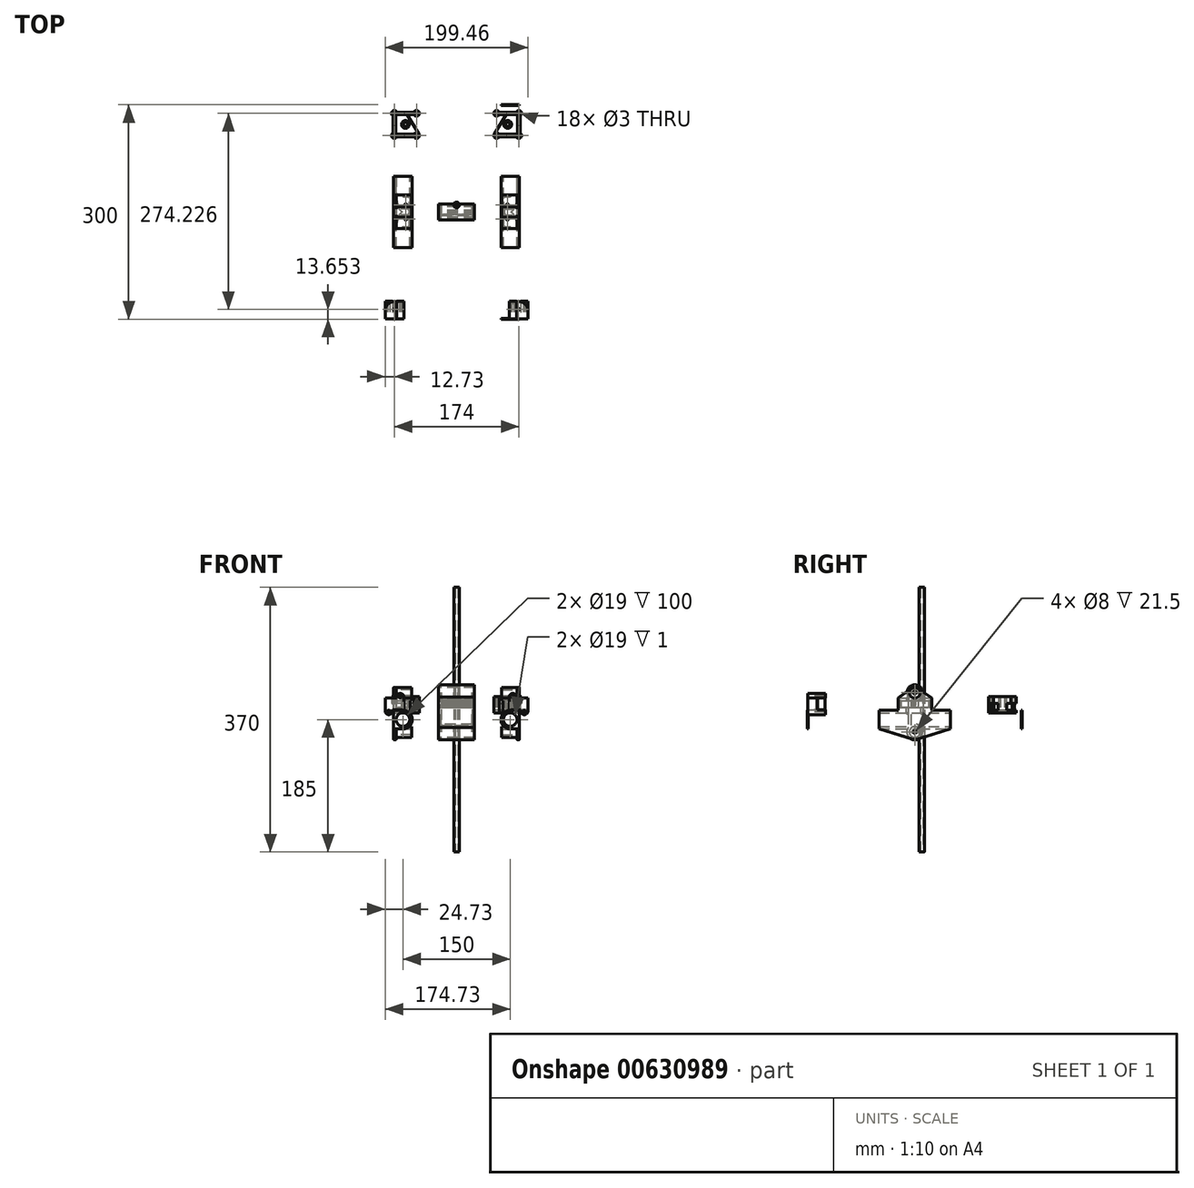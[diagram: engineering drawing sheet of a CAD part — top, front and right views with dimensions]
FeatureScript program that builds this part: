
annotation { "Feature Type Name" : "Feature", "Feature Type Description" : "" }
export const myFeature = defineFeature(function(context is Context, id is Id, definition is map)
    precondition{}
    {
        {
            assignVariable(context, id + "F0", {"variableType" : VariableType.LENGTH, "name" : "Largo", "lengthValue" : 100 * mm});
        }
        {
            assignVariable(context, id + "F1", {"variableType" : VariableType.LENGTH, "name" : "Espesor", "lengthValue" : 3.5 * mm});
        }
        {
            var Q0;
            Q0=qCreatedBy(makeId("Front.planeOp"),FACE);
            var sketch = newSketch(context, id + "F2", { "sketchPlane" : qUnion([Q0])});
            skCircle(sketch, "E0", {"center": v(-75, 0) * mm, "radius": 9.5 * mm});
            skCircle(sketch, "E1", {"center": v(75, 0) * mm, "radius": 9.5 * mm});
            skLineSegment(sketch, "E2", {"start": v(-75, 0) * mm, "end": v(0, 0) * mm, "construction": true});
            skLineSegment(sketch, "E3", {"start": v(0, 0) * mm, "end": v(75, 0) * mm, "construction": true});
            skCircle(sketch, "E4", {"center": v(75, 0) * mm, "radius": 13 * mm, "construction": true});
            skLineSegment(sketch, "E5", {"start": v(88, 0) * mm, "end": v(88, 13) * mm});
            skLineSegment(sketch, "E6", {"start": v(88, 0) * mm, "end": v(88, -13) * mm});
            skLineSegment(sketch, "E7", {"start": v(88, -13) * mm, "end": v(84, -13) * mm});
            skLineSegment(sketch, "E8", {"start": v(84, -13) * mm, "end": v(84, -13) * mm});
            skLineSegment(sketch, "E9", {"start": v(84, -13) * mm, "end": v(75, -13) * mm});
            skLineSegment(sketch, "E10", {"start": v(75, 13) * mm, "end": v(84, 13) * mm});
            skLineSegment(sketch, "E11", {"start": v(84, 13) * mm, "end": v(84, 13) * mm});
            skLineSegment(sketch, "E12", {"start": v(84, 13) * mm, "end": v(88, 13) * mm});
            skArc(sketch, "E13", {"start": v(75, 13) * mm, "mid": v(62, 0) * mm, "end": v(75, -13) * mm});
            skSolve(sketch);
        }
        {
            var Q0;
            Q0=makeQuery(id+"F2.imprint","IMPRINT",FACE,{"disambiguationData":[TD([[makeQuery(id+"F2.imprint","IMPRINT",EDGE,{"derivedFrom":sQuery(id+"F2.wireOp",EDGE,"E1")}),-1.0]])]});
            extrude(context, id + "F3", {"entities" : qUnion([Q0]), "depth" : getVariable(context, 'Largo'), "offsetDistance" : 25 * mm, "symmetric" : true});
        }
        {
            var Q0;
            Q0=makeQuery(id+"F3.opExtrude","SWEPT_FACE",FACE,{"disambiguationData":[OSD([sQuery(id+"F2.wireOp",EDGE,"E5"),sQuery(id+"F2.wireOp",EDGE,"E6")])]});
            var sketch = newSketch(context, id + "F4", { "sketchPlane" : qUnion([Q0])});
            skCircle(sketch, "E14", {"center": v(0, 37.6) * mm, "radius": 2 * mm});
            skCircle(sketch, "E15", {"center": v(0, -17.4) * mm, "radius": 2 * mm});
            skCircle(sketch, "E16", {"center": v(0, -17.4) * mm, "radius": 4 * mm});
            skCircle(sketch, "E17", {"center": v(0, -17.4) * mm, "radius": 7.5 * mm});
            skCircle(sketch, "E18", {"center": v(0, -17.4) * mm, "radius": 10.5 * mm});
            skCircle(sketch, "E19", {"center": v(0, 37.6) * mm, "radius": 4 * mm});
            skCircle(sketch, "E20", {"center": v(0, 37.6) * mm, "radius": 7.5 * mm});
            skCircle(sketch, "E21", {"center": v(0, 37.6) * mm, "radius": 10.5 * mm});
            skLineSegment(sketch, "E22", {"start": v(-50, -13) * mm, "end": v(-3.09, -27.44) * mm});
            skLineSegment(sketch, "E23", {"start": v(50, -13) * mm, "end": v(3.09, -27.44) * mm});
            skLineSegment(sketch, "E24", {"start": v(-50, 13) * mm, "end": v(-6.33, 45.98) * mm});
            skLineSegment(sketch, "E25", {"start": v(50, 13) * mm, "end": v(6.33, 45.98) * mm});
            skLineSegment(sketch, "E26", {"start": v(-7.5, 37.6) * mm, "end": v(-7.5, 28.16) * mm});
            skLineSegment(sketch, "E27", {"start": v(-7.5, 28.16) * mm, "end": v(7.5, 28.16) * mm});
            skLineSegment(sketch, "E28", {"start": v(7.5, 37.6) * mm, "end": v(7.5, 28.16) * mm});
            skSolve(sketch);
        }
        {
            var Q0;
            {var subQ0=sQuery(id+"F4.wireOp",EDGE,"E24");Q0=makeQuery(id+"F4.imprint","IMPRINT",FACE,{"disambiguationData":[TD([[makeQuery(id+"F4.imprint","IMPRINT",EDGE,{"derivedFrom":subQ0}),-1.0]])]});}
            var Q1;
            Q1=makeQuery(id+"F4.imprint","IMPRINT",FACE,{"disambiguationData":[TD([[makeQuery(id+"F4.imprint","IMPRINT",EDGE,{"derivedFrom":sQuery(id+"F4.wireOp",EDGE,"E20")}),-1.0]])]});
            var Q2;
            Q2=makeQuery(id+"F4.imprint","IMPRINT",FACE,{"disambiguationData":[TD([[makeQuery(id+"F4.imprint","IMPRINT",EDGE,{"derivedFrom":sQuery(id+"F4.wireOp",EDGE,"E19")}),-1.0]])]});
            var Q3;
            Q3=makeQuery(id+"F4.imprint","IMPRINT",FACE,{"disambiguationData":[TD([[makeQuery(id+"F4.imprint","IMPRINT",EDGE,{"derivedFrom":sQuery(id+"F4.wireOp",EDGE,"E14")}),-1.0]])]});
            var Q4;
            {var subQ0=sQuery(id+"F4.wireOp",EDGE,"E22");Q4=makeQuery(id+"F4.imprint","IMPRINT",FACE,{"disambiguationData":[TD([[makeQuery(id+"F4.imprint","IMPRINT",EDGE,{"derivedFrom":subQ0}),1.0]])]});}
            var Q5;
            Q5=makeQuery(id+"F4.imprint","IMPRINT",FACE,{"disambiguationData":[TD([[makeQuery(id+"F4.imprint","IMPRINT",EDGE,{"derivedFrom":sQuery(id+"F4.wireOp",EDGE,"E16")}),-1.0]])]});
            var Q6;
            Q6=makeQuery(id+"F4.imprint","IMPRINT",FACE,{"disambiguationData":[TD([[makeQuery(id+"F4.imprint","IMPRINT",EDGE,{"derivedFrom":sQuery(id+"F4.wireOp",EDGE,"E15")}),-1.0]])]});
            var Q7;
            {var subQ0=sQuery(id+"F4.wireOp",EDGE,"E23");Q7=makeQuery(id+"F4.imprint","IMPRINT",FACE,{"disambiguationData":[TD([[makeQuery(id+"F4.imprint","IMPRINT",EDGE,{"derivedFrom":subQ0}),-1.0]])]});}
            var Q8;
            {var subQ0=sQuery(id+"F4.wireOp",EDGE,"E18");var subQ4=makeQuery(id+"F4.imprint","INTERSECT",VERTEX,{"derivedFrom":[subQ0,sQuery(id+"F4.wireOp",EDGE,"E22")]});Q8=makeQuery(id+"F4.imprint","IMPRINT",FACE,{"disambiguationData":[TD([[makeQuery(id+"F4.imprint","IMPRINT",EDGE,{"disambiguationData":[TD([[subQ4,-1.0]])],"derivedFrom":subQ0}),1.0]])]});}
            var Q9;
            {var subQ0=sQuery(id+"F4.wireOp",EDGE,"E26");var subQ1=sQuery(id+"F4.wireOp",EDGE,"E21");var subQ2=makeQuery(id+"F4.imprint","INTERSECT",VERTEX,{"derivedFrom":[subQ1,subQ0]});Q9=makeQuery(id+"F4.imprint","IMPRINT",FACE,{"disambiguationData":[TD([[makeQuery(id+"F4.imprint","IMPRINT",EDGE,{"disambiguationData":[TD([[subQ2,-1.0]])],"derivedFrom":subQ1}),-1.0]])]});}
            var Q10;
            {var subQ0=sQuery(id+"F4.wireOp",EDGE,"E27");var subQ1=sQuery(id+"F4.wireOp",EDGE,"E21");var subQ2=makeQuery(id+"F4.imprint","INTERSECT",VERTEX,{"disambiguationData":[OD(0.0)],"derivedFrom":[subQ1,subQ0]});Q10=makeQuery(id+"F4.imprint","IMPRINT",FACE,{"disambiguationData":[TD([[makeQuery(id+"F4.imprint","IMPRINT",EDGE,{"disambiguationData":[TD([[subQ2,-1.0]])],"derivedFrom":subQ1}),1.0]])]});}
            var Q11;
            {var subQ0=sQuery(id+"F4.wireOp",EDGE,"E27");var subQ1=sQuery(id+"F4.wireOp",EDGE,"E21");var subQ2=makeQuery(id+"F4.imprint","INTERSECT",VERTEX,{"disambiguationData":[OD(1.0)],"derivedFrom":[subQ1,subQ0]});Q11=makeQuery(id+"F4.imprint","IMPRINT",FACE,{"disambiguationData":[TD([[makeQuery(id+"F4.imprint","IMPRINT",EDGE,{"disambiguationData":[TD([[subQ2,-1.0]])],"derivedFrom":subQ1}),-1.0]])]});}
            extrude(context, id + "F5", {"entities" : qUnion([Q0, Q1, Q2, Q3, Q4, Q5, Q6, Q7, Q8, Q9, Q10, Q11]), "operationType" : NewBodyOperationType.ADD, "oppositeDirection" : true, "depth" : getVariable(context, 'Espesor'), "offsetDistance" : 25 * mm});
        }
        {
            var Q0;
            Q0=makeQuery(id+"F3.opExtrude","SWEPT_FACE",FACE,{"disambiguationData":[OSD([sQuery(id+"F2.wireOp",EDGE,"E10"),sQuery(id+"F2.wireOp",EDGE,"E12")])]});
            var sketch = newSketch(context, id + "F6", { "sketchPlane" : qUnion([Q0])});
            skLineSegment(sketch, "E29", {"start": v(84.5, 23.5) * mm, "end": v(63, 23.5) * mm});
            skLineSegment(sketch, "E30", {"start": v(84.5, -23.5) * mm, "end": v(63, -23.5) * mm});
            skLineSegment(sketch, "E31", {"start": v(63, -23.5) * mm, "end": v(63, 23.5) * mm});
            skLineSegment(sketch, "E32", {"start": v(84.5, 23.5) * mm, "end": v(84.5, 0) * mm});
            skLineSegment(sketch, "E33", {"start": v(84.5, 0) * mm, "end": v(84.5, -23.5) * mm});
            skLineSegment(sketch, "E34.bottom", {"start": v(84.5, 10) * mm, "end": v(71, 10) * mm, "construction": true});
            skLineSegment(sketch, "E34.top", {"start": v(84.5, -10) * mm, "end": v(71, -10) * mm, "construction": true});
            skLineSegment(sketch, "E34.left", {"start": v(84.5, 10) * mm, "end": v(84.5, -10) * mm});
            skLineSegment(sketch, "E34.right", {"start": v(71, 10) * mm, "end": v(71, -10) * mm, "construction": true});
            skPoint(sketch, "E34.middle", {"position": v(77.75, 0) * mm});
            skCircle(sketch, "E35", {"center": v(71, 10) * mm, "radius": 9 * mm, "construction": true});
            skCircle(sketch, "E36", {"center": v(71, -10) * mm, "radius": 9 * mm, "construction": true});
            skCircle(sketch, "E37", {"center": v(71, 10) * mm, "radius": 6 * mm, "construction": true});
            skCircle(sketch, "E38", {"center": v(71, -10) * mm, "radius": 6 * mm, "construction": true});
            skCircle(sketch, "E39", {"center": v(71, -10) * mm, "radius": 1.5 * mm});
            skCircle(sketch, "E40", {"center": v(71, 10) * mm, "radius": 1.5 * mm});
            skLineSegment(sketch, "E41", {"start": v(65, -23.5) * mm, "end": v(65, 23.5) * mm});
            skSolve(sketch);
        }
        {
            var Q0;
            {var subQ4=sQuery(id+"F6.wireOp",EDGE,"E41");Q0=makeQuery(id+"F6.imprint","IMPRINT",FACE,{"disambiguationData":[TD([[makeQuery(id+"F6.imprint","IMPRINT",EDGE,{"derivedFrom":subQ4}),-1.0]])]});}
            var Q1;
            {var subQ0=sQuery(id+"F6.wireOp",EDGE,"E32");Q1=makeQuery(id+"F6.imprint","IMPRINT",FACE,{"disambiguationData":[TD([[makeQuery(id+"F6.imprint","IMPRINT",EDGE,{"derivedFrom":subQ0}),1.0]])]});}
            extrude(context, id + "F7", {"entities" : qUnion([Q0, Q1]), "operationType" : NewBodyOperationType.ADD, "oppositeDirection" : true, "depth" : getVariable(context, 'Espesor'), "offsetDistance" : 25 * mm, "hasSecondDirection" : true, "secondDirectionOppositeDirection" : false, "secondDirectionDepth" : 4 * mm});
        }
        {
            var Q0;
            {var subQ0=sQuery(id+"F6.wireOp",EDGE,"E39");var subQ1=makeQuery(id+"F3.opExtrude","SWEPT_EDGE",EDGE,{"disambiguationData":[OSD([sQuery(id+"F2.wireOp",EDGE,"E10"),sQuery(id+"F2.wireOp",EDGE,"E13")])]});var subQ2=makeQuery(id+"F6.imprint","INTERSECT",VERTEX,{"disambiguationData":[OD(0.0)],"derivedFrom":[subQ1,subQ0]});Q0=makeQuery(id+"F6.imprint","IMPRINT",FACE,{"disambiguationData":[TD([[makeQuery(id+"F6.imprint","IMPRINT",EDGE,{"disambiguationData":[TD([[subQ2,-1.0]])],"derivedFrom":subQ0}),1.0]])]});}
            var Q1;
            {var subQ0=sQuery(id+"F6.wireOp",EDGE,"E39");var subQ1=makeQuery(id+"F3.opExtrude","SWEPT_EDGE",EDGE,{"disambiguationData":[OSD([sQuery(id+"F2.wireOp",EDGE,"E10"),sQuery(id+"F2.wireOp",EDGE,"E13")])]});var subQ2=makeQuery(id+"F6.imprint","INTERSECT",VERTEX,{"disambiguationData":[OD(0.0)],"derivedFrom":[subQ1,subQ0]});Q1=makeQuery(id+"F6.imprint","IMPRINT",FACE,{"disambiguationData":[TD([[makeQuery(id+"F6.imprint","IMPRINT",EDGE,{"disambiguationData":[TD([[subQ2,1.0]])],"derivedFrom":subQ0}),1.0]])]});}
            var Q2;
            {var subQ0=sQuery(id+"F6.wireOp",EDGE,"E40");var subQ1=makeQuery(id+"F3.opExtrude","SWEPT_EDGE",EDGE,{"disambiguationData":[OSD([sQuery(id+"F2.wireOp",EDGE,"E10"),sQuery(id+"F2.wireOp",EDGE,"E13")])]});var subQ2=makeQuery(id+"F6.imprint","INTERSECT",VERTEX,{"disambiguationData":[OD(0.0)],"derivedFrom":[subQ1,subQ0]});Q2=makeQuery(id+"F6.imprint","IMPRINT",FACE,{"disambiguationData":[TD([[makeQuery(id+"F6.imprint","IMPRINT",EDGE,{"disambiguationData":[TD([[subQ2,-1.0]])],"derivedFrom":subQ0}),1.0]])]});}
            var Q3;
            {var subQ0=sQuery(id+"F6.wireOp",EDGE,"E40");var subQ1=makeQuery(id+"F3.opExtrude","SWEPT_EDGE",EDGE,{"disambiguationData":[OSD([sQuery(id+"F2.wireOp",EDGE,"E10"),sQuery(id+"F2.wireOp",EDGE,"E13")])]});var subQ2=makeQuery(id+"F6.imprint","INTERSECT",VERTEX,{"disambiguationData":[OD(0.0)],"derivedFrom":[subQ1,subQ0]});Q3=makeQuery(id+"F6.imprint","IMPRINT",FACE,{"disambiguationData":[TD([[makeQuery(id+"F6.imprint","IMPRINT",EDGE,{"disambiguationData":[TD([[subQ2,1.0]])],"derivedFrom":subQ0}),1.0]])]});}
            extrude(context, id + "F8", {"entities" : qUnion([Q0, Q1, Q2, Q3]), "operationType" : NewBodyOperationType.REMOVE, "oppositeDirection" : true, "depth" : 5 * mm, "offsetDistance" : 25 * mm});
        }
        {
            var Q0;
            {var subQ0=sQuery(id+"F6.wireOp",EDGE,"E31");Q0=makeQuery(id+"F6.imprint","IMPRINT",FACE,{"disambiguationData":[TD([[makeQuery(id+"F6.imprint","IMPRINT",EDGE,{"derivedFrom":subQ0}),-1.0]])]});}
            var Q1;
            {var subQ0=sQuery(id+"F6.wireOp",EDGE,"E32");Q1=makeQuery(id+"F6.imprint","IMPRINT",FACE,{"disambiguationData":[TD([[makeQuery(id+"F6.imprint","IMPRINT",EDGE,{"derivedFrom":subQ0}),1.0]])]});}
            var Q2;
            Q2=makeQuery(id+"F6.imprint","IMPRINT",FACE,{"disambiguationData":[TD([[makeQuery(id+"F6.imprint","IMPRINT",EDGE,{"derivedFrom":sQuery(id+"F6.wireOp",EDGE,"E39")}),-1.0]])]});
            extrude(context, id + "F9", {"entities" : qUnion([Q0, Q1, Q2]), "operationType" : NewBodyOperationType.ADD, "depth" : 17 * mm, "offsetDistance" : 25 * mm, "hasSecondDirection" : true, "secondDirectionOppositeDirection" : false, "secondDirectionDepth" : 13.5 * mm});
        }
        {
            var Q0;
            Q0=makeQuery(id+"F2.imprint","IMPRINT",FACE,{"disambiguationData":[TD([[makeQuery(id+"F2.imprint","IMPRINT",EDGE,{"derivedFrom":sQuery(id+"F2.wireOp",EDGE,"E1")}),-1.0]])]});
            extrude(context, id + "F10", {"entities" : qUnion([Q0]), "depth" : 150 * mm, "offsetDistance" : 25 * mm, "hasSecondDirection" : true, "secondDirectionOppositeDirection" : false, "secondDirectionDepth" : 149 * mm});
        }
        {
            var Q0;
            Q0=makeQuery(id+"F2.imprint","IMPRINT",FACE,{"disambiguationData":[TD([[makeQuery(id+"F2.imprint","IMPRINT",EDGE,{"derivedFrom":sQuery(id+"F2.wireOp",EDGE,"E1")}),-1.0]])]});
            extrude(context, id + "F11", {"entities" : qUnion([Q0]), "oppositeDirection" : true, "depth" : 150 * mm, "offsetDistance" : 25 * mm, "hasSecondDirection" : true, "secondDirectionOppositeDirection" : true, "secondDirectionDepth" : 149 * mm});
        }
        {
            var Q0;
            Q0=makeQuery(id+"F10.opExtrude","SWEPT_FACE",FACE,{"disambiguationData":[OSD([sQuery(id+"F2.wireOp",EDGE,"E10"),sQuery(id+"F2.wireOp",EDGE,"E12")])]});
            var sketch = newSketch(context, id + "F12", { "sketchPlane" : qUnion([Q0])});
            skPoint(sketch, "E42", {"position": v(86.73, -136.35) * mm});
            skPoint(sketch, "E43", {"position": v(86.73, -7.67) * mm});
            skLineSegment(sketch, "E44", {"start": v(99.73, -149.85) * mm, "end": v(73.73, -149.85) * mm});
            skLineSegment(sketch, "E45", {"start": v(73.73, -149.85) * mm, "end": v(73.73, -136.35) * mm});
            skLineSegment(sketch, "E46", {"start": v(99.73, -149.85) * mm, "end": v(99.73, -136.35) * mm});
            skCircle(sketch, "E47", {"center": v(86.73, -136.35) * mm, "radius": 9 * mm, "construction": true});
            skArc(sketch, "E48", {"start": v(96.73, -136.35) * mm, "mid": v(86.73, -146.35) * mm, "end": v(76.73, -136.35) * mm});
            skCircle(sketch, "E49", {"center": v(86.73, -136.35) * mm, "radius": 1.5 * mm});
            skArc(sketch, "E50", {"start": v(75.73, -136.35) * mm, "mid": v(86.73, -125.35) * mm, "end": v(97.73, -136.35) * mm, "construction": true});
            skLineSegment(sketch, "E51", {"start": v(76.73, -136.35) * mm, "end": v(76.73, -129.94) * mm});
            skPoint(sketch, "E52", {"position": v(77, -10) * mm});
            skLineSegment(sketch, "E53", {"start": v(76.73, -136.35) * mm, "end": v(76.73, -149.85) * mm, "construction": true});
            skLineSegment(sketch, "E54", {"start": v(96.73, -136.35) * mm, "end": v(96.73, -149.85) * mm, "construction": true});
            skArc(sketch, "E55", {"start": v(99.73, -136.35) * mm, "mid": v(86.73, -125.35) * mm, "end": v(73.73, -136.35) * mm});
            skLineSegment(sketch, "E56", {"start": v(96.73, -136.35) * mm, "end": v(96.73, -129.94) * mm});
            skSolve(sketch);
        }
        {
            var Q0;
            {var subQ5=sQuery(id+"F12.wireOp",EDGE,"E45");Q0=makeQuery(id+"F12.imprint","IMPRINT",FACE,{"disambiguationData":[TD([[makeQuery(id+"F12.imprint","IMPRINT",EDGE,{"derivedFrom":subQ5}),-1.0]])]});}
            var Q1;
            Q1=makeQuery(id+"F12.imprint","IMPRINT",FACE,{"disambiguationData":[TD([[makeQuery(id+"F12.imprint","IMPRINT",EDGE,{"derivedFrom":sQuery(id+"F12.wireOp",EDGE,"E48")}),-1.0]])]});
            var Q2;
            {var subQ0=sQuery(id+"F12.wireOp",EDGE,"E46");Q2=makeQuery(id+"F12.imprint","IMPRINT",FACE,{"disambiguationData":[TD([[makeQuery(id+"F12.imprint","IMPRINT",EDGE,{"derivedFrom":subQ0}),1.0]])]});}
            var Q3;
            {var subQ2=sQuery(id+"F12.wireOp",EDGE,"E48");Q3=makeQuery(id+"F12.imprint","IMPRINT",FACE,{"disambiguationData":[TD([[makeQuery(id+"F12.imprint","IMPRINT",EDGE,{"derivedFrom":subQ2}),1.0]])]});}
            var Q4;
            {var subQ0=sQuery(id+"F12.wireOp",EDGE,"E53");var subQ1=sQuery(id+"F12.wireOp",EDGE,"E44");var subQ2=makeQuery(id+"F12.imprint","INTERSECT",VERTEX,{"derivedFrom":[subQ1,subQ0]});Q4=makeQuery(id+"F12.imprint","IMPRINT",FACE,{"disambiguationData":[TD([[makeQuery(id+"F12.imprint","IMPRINT",EDGE,{"disambiguationData":[TD([[subQ2,1.0]])],"derivedFrom":subQ1}),-1.0]])]});}
            var Q5;
            {var subQ0=sQuery(id+"F12.wireOp",EDGE,"E53");var subQ1=sQuery(id+"F12.wireOp",EDGE,"E44");var subQ2=makeQuery(id+"F12.imprint","INTERSECT",VERTEX,{"derivedFrom":[subQ1,subQ0]});Q5=makeQuery(id+"F12.imprint","IMPRINT",FACE,{"disambiguationData":[TD([[makeQuery(id+"F12.imprint","IMPRINT",EDGE,{"disambiguationData":[TD([[subQ2,-1.0]])],"derivedFrom":subQ1}),-1.0]])]});}
            var Q6;
            {var subQ1=sQuery(id+"F2.wireOp",EDGE,"E12");var subQ4=sQuery(id+"F2.wireOp",EDGE,"E10");var subQ7=makeQuery(id+"F10.opExtrude","CAP_EDGE",EDGE,{"disambiguationData":[OSD([subQ4,subQ1])],"isStart":true});Q6=makeQuery(id+"F12.imprint","IMPRINT",FACE,{"disambiguationData":[TD([[makeQuery(id+"F12.imprint","IMPRINT",EDGE,{"derivedFrom":subQ7}),-1.0]])]});}
            extrude(context, id + "F13", {"entities" : qUnion([Q0, Q1, Q2, Q3, Q4, Q5, Q6]), "operationType" : NewBodyOperationType.ADD, "depth" : 4 * mm, "offsetDistance" : 25 * mm, "hasSecondDirection" : true, "secondDirectionOppositeDirection" : false, "secondDirectionDepth" : 0.5 * mm});
        }
        {
            var Q0;
            {var subQ5=sQuery(id+"F12.wireOp",EDGE,"E45");Q0=makeQuery(id+"F12.imprint","IMPRINT",FACE,{"disambiguationData":[TD([[makeQuery(id+"F12.imprint","IMPRINT",EDGE,{"derivedFrom":subQ5}),-1.0]])]});}
            var Q1;
            {var subQ0=sQuery(id+"F12.wireOp",EDGE,"E46");Q1=makeQuery(id+"F12.imprint","IMPRINT",FACE,{"disambiguationData":[TD([[makeQuery(id+"F12.imprint","IMPRINT",EDGE,{"derivedFrom":subQ0}),1.0]])]});}
            var Q2;
            {var subQ2=sQuery(id+"F12.wireOp",EDGE,"E48");Q2=makeQuery(id+"F12.imprint","IMPRINT",FACE,{"disambiguationData":[TD([[makeQuery(id+"F12.imprint","IMPRINT",EDGE,{"derivedFrom":subQ2}),1.0]])]});}
            var Q3;
            {var subQ0=sQuery(id+"F12.wireOp",EDGE,"E53");var subQ1=sQuery(id+"F12.wireOp",EDGE,"E44");var subQ2=makeQuery(id+"F12.imprint","INTERSECT",VERTEX,{"derivedFrom":[subQ1,subQ0]});Q3=makeQuery(id+"F12.imprint","IMPRINT",FACE,{"disambiguationData":[TD([[makeQuery(id+"F12.imprint","IMPRINT",EDGE,{"disambiguationData":[TD([[subQ2,1.0]])],"derivedFrom":subQ1}),-1.0]])]});}
            var Q4;
            {var subQ1=sQuery(id+"F2.wireOp",EDGE,"E12");var subQ4=sQuery(id+"F2.wireOp",EDGE,"E10");var subQ7=makeQuery(id+"F10.opExtrude","CAP_EDGE",EDGE,{"disambiguationData":[OSD([subQ4,subQ1])],"isStart":true});Q4=makeQuery(id+"F12.imprint","IMPRINT",FACE,{"disambiguationData":[TD([[makeQuery(id+"F12.imprint","IMPRINT",EDGE,{"derivedFrom":subQ7}),-1.0]])]});}
            extrude(context, id + "F14", {"entities" : qUnion([Q0, Q1, Q2, Q3, Q4]), "operationType" : NewBodyOperationType.ADD, "depth" : 13.5 * mm, "offsetDistance" : 25 * mm, "hasSecondDirection" : true, "secondDirectionOppositeDirection" : false, "secondDirectionDepth" : 0.5 * mm});
        }
        {
            var Q0;
            {var subQ5=sQuery(id+"F12.wireOp",EDGE,"E45");Q0=makeQuery(id+"F12.imprint","IMPRINT",FACE,{"disambiguationData":[TD([[makeQuery(id+"F12.imprint","IMPRINT",EDGE,{"derivedFrom":subQ5}),-1.0]])]});}
            var Q1;
            Q1=makeQuery(id+"F12.imprint","IMPRINT",FACE,{"disambiguationData":[TD([[makeQuery(id+"F12.imprint","IMPRINT",EDGE,{"derivedFrom":sQuery(id+"F12.wireOp",EDGE,"E48")}),-1.0]])]});
            var Q2;
            {var subQ0=sQuery(id+"F12.wireOp",EDGE,"E46");Q2=makeQuery(id+"F12.imprint","IMPRINT",FACE,{"disambiguationData":[TD([[makeQuery(id+"F12.imprint","IMPRINT",EDGE,{"derivedFrom":subQ0}),1.0]])]});}
            var Q3;
            {var subQ2=sQuery(id+"F12.wireOp",EDGE,"E48");Q3=makeQuery(id+"F12.imprint","IMPRINT",FACE,{"disambiguationData":[TD([[makeQuery(id+"F12.imprint","IMPRINT",EDGE,{"derivedFrom":subQ2}),1.0]])]});}
            var Q4;
            {var subQ0=sQuery(id+"F12.wireOp",EDGE,"E53");var subQ1=sQuery(id+"F12.wireOp",EDGE,"E44");var subQ2=makeQuery(id+"F12.imprint","INTERSECT",VERTEX,{"derivedFrom":[subQ1,subQ0]});Q4=makeQuery(id+"F12.imprint","IMPRINT",FACE,{"disambiguationData":[TD([[makeQuery(id+"F12.imprint","IMPRINT",EDGE,{"disambiguationData":[TD([[subQ2,1.0]])],"derivedFrom":subQ1}),-1.0]])]});}
            var Q5;
            {var subQ1=sQuery(id+"F2.wireOp",EDGE,"E12");var subQ4=sQuery(id+"F2.wireOp",EDGE,"E10");var subQ7=makeQuery(id+"F10.opExtrude","CAP_EDGE",EDGE,{"disambiguationData":[OSD([subQ4,subQ1])],"isStart":true});Q5=makeQuery(id+"F12.imprint","IMPRINT",FACE,{"disambiguationData":[TD([[makeQuery(id+"F12.imprint","IMPRINT",EDGE,{"derivedFrom":subQ7}),-1.0]])]});}
            extrude(context, id + "F15", {"entities" : qUnion([Q0, Q1, Q2, Q3, Q4, Q5]), "operationType" : NewBodyOperationType.ADD, "depth" : (4 + 9.5 + 3.5) * mm, "offsetDistance" : 25 * mm, "hasSecondDirection" : true, "secondDirectionOppositeDirection" : false, "secondDirectionDepth" : (4 + 9.5) * mm});
        }
        {
            var Q0;
            {var subQ0=sQuery(id+"F12.wireOp",EDGE,"E44");Q0=makeQuery(id+"F15.boolean.opBoolean","MERGE",FACE,{"derivedFrom":[makeQuery(id+"F14.boolean.opBoolean","MERGE",FACE,{"derivedFrom":[makeQuery(id+"F13.opExtrude","SWEPT_FACE",FACE,{"disambiguationData":[OSD([subQ0])]}),makeQuery(id+"F14.opExtrude","SWEPT_FACE",FACE,{"disambiguationData":[OSD([subQ0])]})]}),makeQuery(id+"F15.opExtrude","SWEPT_FACE",FACE,{"disambiguationData":[OSD([subQ0])]})]});}
            var sketch = newSketch(context, id + "F16", { "sketchPlane" : qUnion([Q0])});
            skLineSegment(sketch, "E57", {"start": v(73.73, 31.63) * mm, "end": v(73.73, 30) * mm});
            skLineSegment(sketch, "E58", {"start": v(73.73, 30) * mm, "end": v(83.73, 30) * mm});
            skLineSegment(sketch, "E59", {"start": v(83.73, 30) * mm, "end": v(83.73, 31.63) * mm});
            skCircle(sketch, "E60", {"center": v(78.73, 31.63) * mm, "radius": 1.5 * mm});
            skArc(sketch, "E61", {"start": v(73.73, 31.63) * mm, "mid": v(78.73, 36.63) * mm, "end": v(83.73, 31.63) * mm});
            skPoint(sketch, "E62", {"position": v(75, 0) * mm});
            skLineSegment(sketch, "E63.top", {"start": v(78.73, 11.87) * mm, "end": v(78.95, 11.87) * mm, "construction": true});
            skLineSegment(sketch, "E63.left", {"start": v(78.73, 31.63) * mm, "end": v(78.73, 11.87) * mm, "construction": true});
            skLineSegment(sketch, "E64.bottom", {"start": v(78.73, 11.87) * mm, "end": v(75, 11.87) * mm, "construction": true});
            skLineSegment(sketch, "E64.top", {"start": v(78.73, 0) * mm, "end": v(75, 0) * mm, "construction": true});
            skLineSegment(sketch, "E64.left", {"start": v(78.73, 11.87) * mm, "end": v(78.73, 0) * mm, "construction": true});
            skLineSegment(sketch, "E64.right", {"start": v(75, 11.87) * mm, "end": v(75, 0) * mm, "construction": true});
            skLineSegment(sketch, "E65", {"start": v(89.73, 11.87) * mm, "end": v(89.73, 13.5) * mm});
            skLineSegment(sketch, "E66", {"start": v(89.73, 13.5) * mm, "end": v(99.73, 13.5) * mm});
            skLineSegment(sketch, "E67", {"start": v(99.73, 13.5) * mm, "end": v(99.73, 11.87) * mm});
            skArc(sketch, "E68", {"start": v(99.73, 11.87) * mm, "mid": v(94.73, 6.87) * mm, "end": v(89.73, 11.87) * mm});
            skCircle(sketch, "E69", {"center": v(94.73, 11.87) * mm, "radius": 1.5 * mm});
            skLineSegment(sketch, "E70.bottom", {"start": v(78.73, 11.87) * mm, "end": v(94.73, 11.87) * mm, "construction": true});
            skLineSegment(sketch, "E70.top", {"start": v(78.73, 31.63) * mm, "end": v(94.73, 31.63) * mm, "construction": true});
            skLineSegment(sketch, "E70.left", {"start": v(78.73, 11.87) * mm, "end": v(78.73, 31.63) * mm, "construction": true});
            skLineSegment(sketch, "E70.right", {"start": v(94.73, 11.87) * mm, "end": v(94.73, 31.63) * mm, "construction": true});
            skSolve(sketch);
        }
        {
            var Q0;
            {var subQ2=sQuery(id+"F16.wireOp",EDGE,"E57");Q0=makeQuery(id+"F16.imprint","IMPRINT",FACE,{"disambiguationData":[TD([[makeQuery(id+"F16.imprint","IMPRINT",EDGE,{"derivedFrom":subQ2}),1.0]])]});}
            var Q1;
            {var subQ5=sQuery(id+"F16.wireOp",EDGE,"lFzHnj4Q-87Bt-HTbF-StXR-67TSzxUFeQIK");Q1=makeQuery(id+"F16.imprint","IMPRINT",FACE,{"disambiguationData":[TD([[makeQuery(id+"F16.imprint","IMPRINT",EDGE,{"derivedFrom":subQ5}),1.0]])]});}
            var Q2;
            Q2=makeQuery(id+"F16.imprint","IMPRINT",FACE,{"disambiguationData":[TD([[makeQuery(id+"F16.imprint","IMPRINT",EDGE,{"derivedFrom":sQuery(id+"F16.wireOp",EDGE,"E65")}),-1.0]])]});
            var Q3;
            {var subQ0=sQuery(id+"F16.wireOp",EDGE,"E61");Q3=makeQuery(id+"F16.imprint","IMPRINT",FACE,{"disambiguationData":[TD([[makeQuery(id+"F16.imprint","IMPRINT",EDGE,{"derivedFrom":subQ0}),-1.0]])]});}
            var Q4;
            {var subQ0=sQuery(id+"F16.wireOp",EDGE,"E68");Q4=makeQuery(id+"F16.imprint","IMPRINT",FACE,{"disambiguationData":[TD([[makeQuery(id+"F16.imprint","IMPRINT",EDGE,{"derivedFrom":subQ0}),-1.0]])]});}
            extrude(context, id + "F17", {"entities" : qUnion([Q0, Q1, Q2, Q3, Q4]), "operationType" : NewBodyOperationType.ADD, "oppositeDirection" : true, "depth" : 25 * mm, "offsetDistance" : 25 * mm});
        }
        {
            var Q0;
            {var subQ0=sQuery(id+"F4.wireOp",EDGE,"E16");Q0=makeQuery(id+"F4.imprint","IMPRINT",FACE,{"disambiguationData":[TD([[makeQuery(id+"F4.imprint","IMPRINT",EDGE,{"derivedFrom":subQ0}),-1.0]])]});}
            var Q1;
            {var subQ0=sQuery(id+"F4.wireOp",EDGE,"E17");var subQ1=makeQuery(id+"F3.opExtrude","SWEPT_EDGE",EDGE,{"disambiguationData":[OSD([sQuery(id+"F2.wireOp",EDGE,"E6"),sQuery(id+"F2.wireOp",EDGE,"E7")])]});var subQ2=makeQuery(id+"F4.imprint","INTERSECT",VERTEX,{"disambiguationData":[OD(0.0)],"derivedFrom":[subQ1,subQ0]});Q1=makeQuery(id+"F4.imprint","IMPRINT",FACE,{"disambiguationData":[TD([[makeQuery(id+"F4.imprint","IMPRINT",EDGE,{"disambiguationData":[TD([[subQ2,1.0]])],"derivedFrom":subQ0}),1.0]])]});}
            var Q2;
            Q2=makeQuery(id+"F4.imprint","IMPRINT",FACE,{"disambiguationData":[TD([[makeQuery(id+"F4.imprint","IMPRINT",EDGE,{"derivedFrom":sQuery(id+"F4.wireOp",EDGE,"E19")}),-1.0]])]});
            var Q3;
            {var subQ0=sQuery(id+"F4.wireOp",EDGE,"E26");var subQ1=sQuery(id+"F4.wireOp",EDGE,"E20");var subQ2=makeQuery(id+"F4.imprint","INTERSECT",VERTEX,{"derivedFrom":[subQ1,subQ0]});Q3=makeQuery(id+"F4.imprint","IMPRINT",FACE,{"disambiguationData":[TD([[makeQuery(id+"F4.imprint","IMPRINT",EDGE,{"disambiguationData":[TD([[subQ2,-1.0]])],"derivedFrom":subQ1}),-1.0]])]});}
            var Q4;
            {var subQ0=sQuery(id+"F4.wireOp",EDGE,"E27");var subQ1=sQuery(id+"F4.wireOp",EDGE,"E21");var subQ2=makeQuery(id+"F4.imprint","INTERSECT",VERTEX,{"disambiguationData":[OD(1.0)],"derivedFrom":[subQ1,subQ0]});Q4=makeQuery(id+"F4.imprint","IMPRINT",FACE,{"disambiguationData":[TD([[makeQuery(id+"F4.imprint","IMPRINT",EDGE,{"disambiguationData":[TD([[subQ2,-1.0]])],"derivedFrom":subQ1}),-1.0]])]});}
            var Q5;
            {var subQ0=sQuery(id+"F4.wireOp",EDGE,"E26");var subQ1=sQuery(id+"F4.wireOp",EDGE,"E21");var subQ2=makeQuery(id+"F4.imprint","INTERSECT",VERTEX,{"derivedFrom":[subQ1,subQ0]});Q5=makeQuery(id+"F4.imprint","IMPRINT",FACE,{"disambiguationData":[TD([[makeQuery(id+"F4.imprint","IMPRINT",EDGE,{"disambiguationData":[TD([[subQ2,-1.0]])],"derivedFrom":subQ1}),-1.0]])]});}
            extrude(context, id + "F18", {"entities" : qUnion([Q0, Q1, Q2, Q3, Q4, Q5]), "operationType" : NewBodyOperationType.ADD, "oppositeDirection" : true, "depth" : 25 * mm, "offsetDistance" : 25 * mm});
        }
        {
            var Q0;
            Q0=makeQuery(id+"F11.opExtrude","SWEPT_FACE",FACE,{"disambiguationData":[OSD([sQuery(id+"F2.wireOp",EDGE,"E10"),sQuery(id+"F2.wireOp",EDGE,"E12")])]});
            var sketch = newSketch(context, id + "F19", { "sketchPlane" : qUnion([Q0])});
            skPoint(sketch, "E71", {"position": v(71.5, 10) * mm});
            skPoint(sketch, "E72", {"position": v(77, 10) * mm});
            skPoint(sketch, "E73", {"position": v(71.5, 122.38) * mm});
            skLineSegment(sketch, "E74.bottom", {"start": v(50, 143.88) * mm, "end": v(93, 143.88) * mm});
            skLineSegment(sketch, "E74.top", {"start": v(50, 100.88) * mm, "end": v(93, 100.88) * mm});
            skLineSegment(sketch, "E74.left", {"start": v(50, 143.88) * mm, "end": v(50, 100.88) * mm});
            skLineSegment(sketch, "E74.right", {"start": v(93, 143.88) * mm, "end": v(93, 100.88) * mm});
            skLineSegment(sketch, "E75.bottom", {"start": v(56, 137.88) * mm, "end": v(87, 137.88) * mm, "construction": true});
            skLineSegment(sketch, "E75.top", {"start": v(56, 106.88) * mm, "end": v(87, 106.88) * mm, "construction": true});
            skLineSegment(sketch, "E75.left", {"start": v(56, 137.88) * mm, "end": v(56, 106.88) * mm, "construction": true});
            skLineSegment(sketch, "E75.right", {"start": v(87, 137.88) * mm, "end": v(87, 106.88) * mm, "construction": true});
            skCircle(sketch, "E76", {"center": v(56, 137.88) * mm, "radius": 1.5 * mm});
            skCircle(sketch, "E77", {"center": v(87, 137.88) * mm, "radius": 1.5 * mm});
            skCircle(sketch, "E78", {"center": v(87, 106.88) * mm, "radius": 1.5 * mm});
            skCircle(sketch, "E79", {"center": v(56, 106.88) * mm, "radius": 1.5 * mm});
            skCircle(sketch, "E80", {"center": v(71.5, 122.38) * mm, "radius": 5.5 * mm});
            skCircle(sketch, "E81", {"center": v(71.5, 122.38) * mm, "radius": 7.5 * mm});
            skLineSegment(sketch, "E82", {"start": v(71.5, 122.38) * mm, "end": v(71.5, 10) * mm, "construction": true});
            skCircle(sketch, "E83", {"center": v(87, 137.88) * mm, "radius": 7.5 * mm});
            skCircle(sketch, "E84", {"center": v(87, 137.88) * mm, "radius": 6 * mm});
            skLineSegment(sketch, "E85.bottom", {"start": v(87, 137.88) * mm, "end": v(101, 137.88) * mm, "construction": true});
            skLineSegment(sketch, "E85.top", {"start": v(87, 151.88) * mm, "end": v(101, 151.88) * mm, "construction": true});
            skLineSegment(sketch, "E85.left", {"start": v(87, 137.88) * mm, "end": v(87, 151.88) * mm, "construction": true});
            skLineSegment(sketch, "E85.right", {"start": v(101, 137.88) * mm, "end": v(101, 151.88) * mm, "construction": true});
            skLineSegment(sketch, "E86.bottom", {"start": v(101, 151.88) * mm, "end": v(98.5, 151.88) * mm});
            skLineSegment(sketch, "E86.left", {"start": v(101, 151.88) * mm, "end": v(101, 149.38) * mm});
            skCircle(sketch, "E87", {"center": v(56, 137.88) * mm, "radius": 4 * mm});
            skCircle(sketch, "E88", {"center": v(87, 137.88) * mm, "radius": 4 * mm});
            skCircle(sketch, "E89", {"center": v(87, 106.88) * mm, "radius": 4 * mm});
            skLineSegment(sketch, "E90.bottom", {"start": v(59.6, 136.13) * mm, "end": v(83.4, 136.13) * mm});
            skLineSegment(sketch, "E90.top", {"start": v(59.6, 139.63) * mm, "end": v(83.4, 139.63) * mm});
            skLineSegment(sketch, "E90.left", {"start": v(59.6, 136.13) * mm, "end": v(59.6, 139.63) * mm, "construction": true});
            skLineSegment(sketch, "E90.right", {"start": v(83.4, 136.13) * mm, "end": v(83.4, 139.63) * mm, "construction": true});
            skPoint(sketch, "E90.middle", {"position": v(71.5, 137.88) * mm});
            skLineSegment(sketch, "E91.bottom", {"start": v(85.25, 134.28) * mm, "end": v(88.75, 134.28) * mm, "construction": true});
            skLineSegment(sketch, "E91.top", {"start": v(85.25, 110.48) * mm, "end": v(88.75, 110.48) * mm, "construction": true});
            skLineSegment(sketch, "E91.left", {"start": v(85.25, 134.28) * mm, "end": v(85.25, 110.48) * mm});
            skLineSegment(sketch, "E91.right", {"start": v(88.75, 134.28) * mm, "end": v(88.75, 110.48) * mm});
            skPoint(sketch, "E91.middle", {"position": v(87, 122.38) * mm});
            skCircle(sketch, "E92", {"center": v(87, 137.88) * mm, "radius": 9.5 * mm});
            skCircle(sketch, "E93", {"center": v(87, 106.88) * mm, "radius": 9.5 * mm});
            skCircle(sketch, "E94", {"center": v(56, 106.88) * mm, "radius": 4 * mm});
            skLineSegment(sketch, "E95.bottom", {"start": v(59.6, 105.13) * mm, "end": v(83.4, 105.13) * mm});
            skLineSegment(sketch, "E95.top", {"start": v(59.6, 108.63) * mm, "end": v(83.4, 108.63) * mm});
            skLineSegment(sketch, "E95.left", {"start": v(59.6, 105.13) * mm, "end": v(59.6, 108.63) * mm, "construction": true});
            skLineSegment(sketch, "E95.right", {"start": v(83.4, 105.13) * mm, "end": v(83.4, 108.63) * mm, "construction": true});
            skPoint(sketch, "E95.middle", {"position": v(71.5, 106.88) * mm});
            skCircle(sketch, "E96", {"center": v(71.5, 122.38) * mm, "radius": 3 * mm});
            skLineSegment(sketch, "E97", {"start": v(71.5, 139.63) * mm, "end": v(52.6, 108.98) * mm});
            skSolve(sketch);
        }
        {
            var Q0;
            Q0=makeQuery(id+"F19.imprint","IMPRINT",FACE,{"disambiguationData":[TD([[makeQuery(id+"F19.imprint","IMPRINT",EDGE,{"derivedFrom":sQuery(id+"F19.wireOp",EDGE,"E80")}),1.0]])]});
            var Q1;
            Q1=makeQuery(id+"F19.imprint","IMPRINT",FACE,{"disambiguationData":[TD([[makeQuery(id+"F19.imprint","IMPRINT",EDGE,{"derivedFrom":sQuery(id+"F19.wireOp",EDGE,"E77")}),-1.0]])]});
            var Q2;
            {var subQ0=sQuery(id+"F19.wireOp",EDGE,"E90.top");var subQ1=sQuery(id+"F19.wireOp",EDGE,"E84");var subQ2=makeQuery(id+"F19.imprint","INTERSECT",VERTEX,{"derivedFrom":[subQ1,subQ0]});Q2=makeQuery(id+"F19.imprint","IMPRINT",FACE,{"disambiguationData":[TD([[makeQuery(id+"F19.imprint","IMPRINT",EDGE,{"disambiguationData":[TD([[subQ2,-1.0]])],"derivedFrom":subQ1}),1.0]])]});}
            var Q3;
            {var subQ0=sQuery(id+"F19.wireOp",EDGE,"E91.left");var subQ1=sQuery(id+"F19.wireOp",EDGE,"E84");var subQ2=makeQuery(id+"F19.imprint","INTERSECT",VERTEX,{"derivedFrom":[subQ1,subQ0]});Q3=makeQuery(id+"F19.imprint","IMPRINT",FACE,{"disambiguationData":[TD([[makeQuery(id+"F19.imprint","IMPRINT",EDGE,{"disambiguationData":[TD([[subQ2,-1.0]])],"derivedFrom":subQ1}),1.0]])]});}
            var Q4;
            {var subQ0=sQuery(id+"F19.wireOp",EDGE,"E92");var subQ1=sQuery(id+"F19.wireOp",EDGE,"E91.left");var subQ2=makeQuery(id+"F19.imprint","INTERSECT",VERTEX,{"derivedFrom":[subQ1,subQ0]});Q4=makeQuery(id+"F19.imprint","IMPRINT",FACE,{"disambiguationData":[TD([[makeQuery(id+"F19.imprint","IMPRINT",EDGE,{"disambiguationData":[TD([[subQ2,-1.0]])],"derivedFrom":subQ1}),1.0]])]});}
            var Q5;
            {var subQ0=sQuery(id+"F19.wireOp",EDGE,"E95.bottom");var subQ1=sQuery(id+"F19.wireOp",EDGE,"E89");var subQ2=makeQuery(id+"F19.imprint","INTERSECT",VERTEX,{"derivedFrom":[subQ1,subQ0]});Q5=makeQuery(id+"F19.imprint","IMPRINT",FACE,{"disambiguationData":[TD([[makeQuery(id+"F19.imprint","IMPRINT",EDGE,{"disambiguationData":[TD([[subQ2,1.0]])],"derivedFrom":subQ1}),-1.0]])]});}
            var Q6;
            {var subQ0=sQuery(id+"F19.wireOp",EDGE,"E95.top");var subQ1=sQuery(id+"F19.wireOp",EDGE,"E93");var subQ2=makeQuery(id+"F19.imprint","INTERSECT",VERTEX,{"derivedFrom":[subQ1,subQ0]});Q6=makeQuery(id+"F19.imprint","IMPRINT",FACE,{"disambiguationData":[TD([[makeQuery(id+"F19.imprint","IMPRINT",EDGE,{"disambiguationData":[TD([[subQ2,-1.0]])],"derivedFrom":subQ1}),-1.0]])]});}
            var Q7;
            Q7=makeQuery(id+"F19.imprint","IMPRINT",FACE,{"disambiguationData":[TD([[makeQuery(id+"F19.imprint","IMPRINT",EDGE,{"derivedFrom":sQuery(id+"F19.wireOp",EDGE,"E79")}),-1.0]])]});
            var Q8;
            Q8=makeQuery(id+"F19.imprint","IMPRINT",FACE,{"disambiguationData":[TD([[makeQuery(id+"F19.imprint","IMPRINT",EDGE,{"derivedFrom":sQuery(id+"F19.wireOp",EDGE,"E78")}),-1.0]])]});
            var Q9;
            {var subQ0=sQuery(id+"F19.wireOp",EDGE,"E91.left");var subQ1=sQuery(id+"F19.wireOp",EDGE,"E89");var subQ2=makeQuery(id+"F19.imprint","INTERSECT",VERTEX,{"derivedFrom":[subQ1,subQ0]});Q9=makeQuery(id+"F19.imprint","IMPRINT",FACE,{"disambiguationData":[TD([[makeQuery(id+"F19.imprint","IMPRINT",EDGE,{"disambiguationData":[TD([[subQ2,1.0]])],"derivedFrom":subQ1}),-1.0]])]});}
            var Q10;
            Q10=makeQuery(id+"F19.imprint","IMPRINT",FACE,{"disambiguationData":[TD([[makeQuery(id+"F19.imprint","IMPRINT",EDGE,{"derivedFrom":sQuery(id+"F19.wireOp",EDGE,"E76")}),-1.0]])]});
            var Q11;
            {var subQ0=sQuery(id+"F19.wireOp",EDGE,"E90.bottom");var subQ1=sQuery(id+"F19.wireOp",EDGE,"E87");var subQ2=makeQuery(id+"F19.imprint","INTERSECT",VERTEX,{"derivedFrom":[subQ1,subQ0]});Q11=makeQuery(id+"F19.imprint","IMPRINT",FACE,{"disambiguationData":[TD([[makeQuery(id+"F19.imprint","IMPRINT",EDGE,{"disambiguationData":[TD([[subQ2,-1.0]])],"derivedFrom":subQ1}),-1.0]])]});}
            var Q12;
            {var subQ0=sQuery(id+"F19.wireOp",EDGE,"E90.top");var subQ1=sQuery(id+"F19.wireOp",EDGE,"E83");var subQ2=makeQuery(id+"F19.imprint","INTERSECT",VERTEX,{"derivedFrom":[subQ1,subQ0]});Q12=makeQuery(id+"F19.imprint","IMPRINT",FACE,{"disambiguationData":[TD([[makeQuery(id+"F19.imprint","IMPRINT",EDGE,{"disambiguationData":[TD([[subQ2,-1.0]])],"derivedFrom":subQ1}),-1.0]])]});}
            var Q13;
            {var subQ0=sQuery(id+"F19.wireOp",EDGE,"E90.top");var subQ1=sQuery(id+"F19.wireOp",EDGE,"E83");var subQ2=makeQuery(id+"F19.imprint","INTERSECT",VERTEX,{"derivedFrom":[subQ1,subQ0]});Q13=makeQuery(id+"F19.imprint","IMPRINT",FACE,{"disambiguationData":[TD([[makeQuery(id+"F19.imprint","IMPRINT",EDGE,{"disambiguationData":[TD([[subQ2,-1.0]])],"derivedFrom":subQ1}),1.0]])]});}
            var Q14;
            {var subQ0=sQuery(id+"F19.wireOp",EDGE,"E91.left");var subQ1=sQuery(id+"F19.wireOp",EDGE,"E83");var subQ2=makeQuery(id+"F19.imprint","INTERSECT",VERTEX,{"derivedFrom":[subQ1,subQ0]});Q14=makeQuery(id+"F19.imprint","IMPRINT",FACE,{"disambiguationData":[TD([[makeQuery(id+"F19.imprint","IMPRINT",EDGE,{"disambiguationData":[TD([[subQ2,-1.0]])],"derivedFrom":subQ1}),1.0]])]});}
            var Q15;
            {var subQ0=sQuery(id+"F19.wireOp",EDGE,"E91.left");var subQ1=sQuery(id+"F19.wireOp",EDGE,"E83");var subQ2=makeQuery(id+"F19.imprint","INTERSECT",VERTEX,{"derivedFrom":[subQ1,subQ0]});Q15=makeQuery(id+"F19.imprint","IMPRINT",FACE,{"disambiguationData":[TD([[makeQuery(id+"F19.imprint","IMPRINT",EDGE,{"disambiguationData":[TD([[subQ2,-1.0]])],"derivedFrom":subQ1}),-1.0]])]});}
            var Q16;
            {var subQ0=sQuery(id+"F19.wireOp",EDGE,"DqG3VXCJ-E9Pa-22pF-3nJk-MnPQh88JCoLb");Q16=makeQuery(id+"F19.imprint","IMPRINT",FACE,{"disambiguationData":[TD([[makeQuery(id+"F19.imprint","IMPRINT",EDGE,{"derivedFrom":subQ0}),-1.0]])]});}
            var Q17;
            {var subQ0=sQuery(id+"F19.wireOp",EDGE,"E97");var subQ1=sQuery(id+"F19.wireOp",EDGE,"E90.bottom");var subQ2=makeQuery(id+"F19.imprint","INTERSECT",VERTEX,{"derivedFrom":[subQ1,subQ0]});Q17=makeQuery(id+"F19.imprint","IMPRINT",FACE,{"disambiguationData":[TD([[makeQuery(id+"F19.imprint","IMPRINT",EDGE,{"disambiguationData":[TD([[subQ2,-1.0]])],"derivedFrom":subQ1}),1.0]])]});}
            extrude(context, id + "F20", {"entities" : qUnion([Q0, Q1, Q2, Q3, Q4, Q5, Q6, Q7, Q8, Q9, Q10, Q11, Q12, Q13, Q14, Q15, Q16, Q17]), "depth" : 19 * mm, "offsetDistance" : 25 * mm});
        }
        {
            var Q0;
            Q0=makeQuery(id+"F19.imprint","IMPRINT",FACE,{"disambiguationData":[TD([[makeQuery(id+"F19.imprint","IMPRINT",EDGE,{"derivedFrom":sQuery(id+"F19.wireOp",EDGE,"E79")}),-1.0]])]});
            var Q1;
            {var subQ0=sQuery(id+"F19.wireOp",EDGE,"E95.top");var subQ1=sQuery(id+"F19.wireOp",EDGE,"E93");var subQ2=makeQuery(id+"F19.imprint","INTERSECT",VERTEX,{"derivedFrom":[subQ1,subQ0]});Q1=makeQuery(id+"F19.imprint","IMPRINT",FACE,{"disambiguationData":[TD([[makeQuery(id+"F19.imprint","IMPRINT",EDGE,{"disambiguationData":[TD([[subQ2,-1.0]])],"derivedFrom":subQ1}),-1.0]])]});}
            var Q2;
            Q2=makeQuery(id+"F19.imprint","IMPRINT",FACE,{"disambiguationData":[TD([[makeQuery(id+"F19.imprint","IMPRINT",EDGE,{"derivedFrom":sQuery(id+"F19.wireOp",EDGE,"E78")}),-1.0]])]});
            var Q3;
            {var subQ0=sQuery(id+"F19.wireOp",EDGE,"E91.left");var subQ1=sQuery(id+"F19.wireOp",EDGE,"E89");var subQ2=makeQuery(id+"F19.imprint","INTERSECT",VERTEX,{"derivedFrom":[subQ1,subQ0]});Q3=makeQuery(id+"F19.imprint","IMPRINT",FACE,{"disambiguationData":[TD([[makeQuery(id+"F19.imprint","IMPRINT",EDGE,{"disambiguationData":[TD([[subQ2,1.0]])],"derivedFrom":subQ1}),-1.0]])]});}
            var Q4;
            {var subQ0=sQuery(id+"F19.wireOp",EDGE,"E92");var subQ1=sQuery(id+"F19.wireOp",EDGE,"E91.left");var subQ2=makeQuery(id+"F19.imprint","INTERSECT",VERTEX,{"derivedFrom":[subQ1,subQ0]});Q4=makeQuery(id+"F19.imprint","IMPRINT",FACE,{"disambiguationData":[TD([[makeQuery(id+"F19.imprint","IMPRINT",EDGE,{"disambiguationData":[TD([[subQ2,-1.0]])],"derivedFrom":subQ1}),1.0]])]});}
            var Q5;
            {var subQ0=sQuery(id+"F19.wireOp",EDGE,"E91.left");var subQ1=sQuery(id+"F19.wireOp",EDGE,"E83");var subQ2=makeQuery(id+"F19.imprint","INTERSECT",VERTEX,{"derivedFrom":[subQ1,subQ0]});Q5=makeQuery(id+"F19.imprint","IMPRINT",FACE,{"disambiguationData":[TD([[makeQuery(id+"F19.imprint","IMPRINT",EDGE,{"disambiguationData":[TD([[subQ2,-1.0]])],"derivedFrom":subQ1}),-1.0]])]});}
            var Q6;
            {var subQ0=sQuery(id+"F19.wireOp",EDGE,"E91.left");var subQ1=sQuery(id+"F19.wireOp",EDGE,"E83");var subQ2=makeQuery(id+"F19.imprint","INTERSECT",VERTEX,{"derivedFrom":[subQ1,subQ0]});Q6=makeQuery(id+"F19.imprint","IMPRINT",FACE,{"disambiguationData":[TD([[makeQuery(id+"F19.imprint","IMPRINT",EDGE,{"disambiguationData":[TD([[subQ2,-1.0]])],"derivedFrom":subQ1}),1.0]])]});}
            var Q7;
            {var subQ0=sQuery(id+"F19.wireOp",EDGE,"E91.left");var subQ1=sQuery(id+"F19.wireOp",EDGE,"E84");var subQ2=makeQuery(id+"F19.imprint","INTERSECT",VERTEX,{"derivedFrom":[subQ1,subQ0]});Q7=makeQuery(id+"F19.imprint","IMPRINT",FACE,{"disambiguationData":[TD([[makeQuery(id+"F19.imprint","IMPRINT",EDGE,{"disambiguationData":[TD([[subQ2,-1.0]])],"derivedFrom":subQ1}),1.0]])]});}
            var Q8;
            Q8=makeQuery(id+"F19.imprint","IMPRINT",FACE,{"disambiguationData":[TD([[makeQuery(id+"F19.imprint","IMPRINT",EDGE,{"derivedFrom":sQuery(id+"F19.wireOp",EDGE,"E77")}),-1.0]])]});
            var Q9;
            {var subQ0=sQuery(id+"F19.wireOp",EDGE,"E90.top");var subQ1=sQuery(id+"F19.wireOp",EDGE,"E84");var subQ2=makeQuery(id+"F19.imprint","INTERSECT",VERTEX,{"derivedFrom":[subQ1,subQ0]});Q9=makeQuery(id+"F19.imprint","IMPRINT",FACE,{"disambiguationData":[TD([[makeQuery(id+"F19.imprint","IMPRINT",EDGE,{"disambiguationData":[TD([[subQ2,-1.0]])],"derivedFrom":subQ1}),1.0]])]});}
            var Q10;
            {var subQ0=sQuery(id+"F19.wireOp",EDGE,"E90.top");var subQ1=sQuery(id+"F19.wireOp",EDGE,"E83");var subQ2=makeQuery(id+"F19.imprint","INTERSECT",VERTEX,{"derivedFrom":[subQ1,subQ0]});Q10=makeQuery(id+"F19.imprint","IMPRINT",FACE,{"disambiguationData":[TD([[makeQuery(id+"F19.imprint","IMPRINT",EDGE,{"disambiguationData":[TD([[subQ2,-1.0]])],"derivedFrom":subQ1}),-1.0]])]});}
            var Q11;
            {var subQ0=sQuery(id+"F19.wireOp",EDGE,"E90.top");var subQ1=sQuery(id+"F19.wireOp",EDGE,"E83");var subQ2=makeQuery(id+"F19.imprint","INTERSECT",VERTEX,{"derivedFrom":[subQ1,subQ0]});Q11=makeQuery(id+"F19.imprint","IMPRINT",FACE,{"disambiguationData":[TD([[makeQuery(id+"F19.imprint","IMPRINT",EDGE,{"disambiguationData":[TD([[subQ2,-1.0]])],"derivedFrom":subQ1}),1.0]])]});}
            var Q12;
            {var subQ0=sQuery(id+"F19.wireOp",EDGE,"E95.bottom");var subQ1=sQuery(id+"F19.wireOp",EDGE,"E89");var subQ2=makeQuery(id+"F19.imprint","INTERSECT",VERTEX,{"derivedFrom":[subQ1,subQ0]});Q12=makeQuery(id+"F19.imprint","IMPRINT",FACE,{"disambiguationData":[TD([[makeQuery(id+"F19.imprint","IMPRINT",EDGE,{"disambiguationData":[TD([[subQ2,1.0]])],"derivedFrom":subQ1}),-1.0]])]});}
            var Q13;
            {var subQ0=sQuery(id+"F19.wireOp",EDGE,"DqG3VXCJ-E9Pa-22pF-3nJk-MnPQh88JCoLb");Q13=makeQuery(id+"F19.imprint","IMPRINT",FACE,{"disambiguationData":[TD([[makeQuery(id+"F19.imprint","IMPRINT",EDGE,{"derivedFrom":subQ0}),-1.0]])]});}
            var Q14;
            {var subQ0=sQuery(id+"F19.wireOp",EDGE,"E97");var subQ1=sQuery(id+"F19.wireOp",EDGE,"E90.bottom");var subQ2=makeQuery(id+"F19.imprint","INTERSECT",VERTEX,{"derivedFrom":[subQ1,subQ0]});Q14=makeQuery(id+"F19.imprint","IMPRINT",FACE,{"disambiguationData":[TD([[makeQuery(id+"F19.imprint","IMPRINT",EDGE,{"disambiguationData":[TD([[subQ2,-1.0]])],"derivedFrom":subQ1}),1.0]])]});}
            var Q15;
            Q15=makeQuery(id+"F19.imprint","IMPRINT",FACE,{"disambiguationData":[TD([[makeQuery(id+"F19.imprint","IMPRINT",EDGE,{"derivedFrom":sQuery(id+"F19.wireOp",EDGE,"E81")}),-1.0]])]});
            var Q16;
            Q16=makeQuery(id+"F19.imprint","IMPRINT",FACE,{"disambiguationData":[TD([[makeQuery(id+"F19.imprint","IMPRINT",EDGE,{"derivedFrom":sQuery(id+"F19.wireOp",EDGE,"E80")}),-1.0]])]});
            var Q17;
            Q17=makeQuery(id+"F19.imprint","IMPRINT",FACE,{"disambiguationData":[TD([[makeQuery(id+"F19.imprint","IMPRINT",EDGE,{"derivedFrom":sQuery(id+"F19.wireOp",EDGE,"E80")}),1.0]])]});
            var Q18;
            {var subQ0=sQuery(id+"F19.wireOp",EDGE,"E90.bottom");var subQ1=sQuery(id+"F19.wireOp",EDGE,"E83");var subQ2=makeQuery(id+"F19.imprint","INTERSECT",VERTEX,{"derivedFrom":[subQ1,subQ0]});Q18=makeQuery(id+"F19.imprint","IMPRINT",FACE,{"disambiguationData":[TD([[makeQuery(id+"F19.imprint","IMPRINT",EDGE,{"disambiguationData":[TD([[subQ2,-1.0]])],"derivedFrom":subQ1}),-1.0]])]});}
            var Q19;
            {var subQ0=sQuery(id+"F19.wireOp",EDGE,"E90.bottom");var subQ1=sQuery(id+"F19.wireOp",EDGE,"E83");var subQ2=makeQuery(id+"F19.imprint","INTERSECT",VERTEX,{"derivedFrom":[subQ1,subQ0]});Q19=makeQuery(id+"F19.imprint","IMPRINT",FACE,{"disambiguationData":[TD([[makeQuery(id+"F19.imprint","IMPRINT",EDGE,{"disambiguationData":[TD([[subQ2,-1.0]])],"derivedFrom":subQ1}),1.0]])]});}
            var Q20;
            {var subQ0=sQuery(id+"F19.wireOp",EDGE,"E90.bottom");var subQ1=sQuery(id+"F19.wireOp",EDGE,"E84");var subQ2=makeQuery(id+"F19.imprint","INTERSECT",VERTEX,{"derivedFrom":[subQ1,subQ0]});Q20=makeQuery(id+"F19.imprint","IMPRINT",FACE,{"disambiguationData":[TD([[makeQuery(id+"F19.imprint","IMPRINT",EDGE,{"disambiguationData":[TD([[subQ2,-1.0]])],"derivedFrom":subQ1}),1.0]])]});}
            var Q21;
            {var subQ0=sQuery(id+"F19.wireOp",EDGE,"E91.left");var subQ1=sQuery(id+"F19.wireOp",EDGE,"E89");var subQ2=makeQuery(id+"F19.imprint","INTERSECT",VERTEX,{"derivedFrom":[subQ1,subQ0]});Q21=makeQuery(id+"F19.imprint","IMPRINT",FACE,{"disambiguationData":[TD([[makeQuery(id+"F19.imprint","IMPRINT",EDGE,{"disambiguationData":[TD([[subQ2,-1.0]])],"derivedFrom":subQ1}),-1.0]])]});}
            extrude(context, id + "F21", {"entities" : qUnion([Q0, Q1, Q2, Q3, Q4, Q5, Q6, Q7, Q8, Q9, Q10, Q11, Q12, Q13, Q14, Q15, Q16, Q17, Q18, Q19, Q20, Q21]), "operationType" : NewBodyOperationType.ADD, "oppositeDirection" : true, "depth" : getVariable(context, 'Espesor'), "offsetDistance" : 25 * mm});
        }
        {
            var Q0;
            {var subQ0=sQuery(id+"F19.wireOp",EDGE,"E95.bottom");var subQ1=sQuery(id+"F19.wireOp",EDGE,"E89");var subQ2=makeQuery(id+"F19.imprint","INTERSECT",VERTEX,{"derivedFrom":[subQ1,subQ0]});Q0=makeQuery(id+"F19.imprint","IMPRINT",FACE,{"disambiguationData":[TD([[makeQuery(id+"F19.imprint","IMPRINT",EDGE,{"disambiguationData":[TD([[subQ2,1.0]])],"derivedFrom":subQ1}),-1.0]])]});}
            var Q1;
            Q1=makeQuery(id+"F19.imprint","IMPRINT",FACE,{"disambiguationData":[TD([[makeQuery(id+"F19.imprint","IMPRINT",EDGE,{"derivedFrom":sQuery(id+"F19.wireOp",EDGE,"E78")}),-1.0]])]});
            var Q2;
            {var subQ0=sQuery(id+"F19.wireOp",EDGE,"E91.left");var subQ1=sQuery(id+"F19.wireOp",EDGE,"E89");var subQ2=makeQuery(id+"F19.imprint","INTERSECT",VERTEX,{"derivedFrom":[subQ1,subQ0]});Q2=makeQuery(id+"F19.imprint","IMPRINT",FACE,{"disambiguationData":[TD([[makeQuery(id+"F19.imprint","IMPRINT",EDGE,{"disambiguationData":[TD([[subQ2,1.0]])],"derivedFrom":subQ1}),-1.0]])]});}
            var Q3;
            Q3=makeQuery(id+"F19.imprint","IMPRINT",FACE,{"disambiguationData":[TD([[makeQuery(id+"F19.imprint","IMPRINT",EDGE,{"derivedFrom":sQuery(id+"F19.wireOp",EDGE,"E77")}),-1.0]])]});
            var Q4;
            {var subQ0=sQuery(id+"F19.wireOp",EDGE,"E90.top");var subQ1=sQuery(id+"F19.wireOp",EDGE,"E84");var subQ2=makeQuery(id+"F19.imprint","INTERSECT",VERTEX,{"derivedFrom":[subQ1,subQ0]});Q4=makeQuery(id+"F19.imprint","IMPRINT",FACE,{"disambiguationData":[TD([[makeQuery(id+"F19.imprint","IMPRINT",EDGE,{"disambiguationData":[TD([[subQ2,-1.0]])],"derivedFrom":subQ1}),1.0]])]});}
            var Q5;
            {var subQ0=sQuery(id+"F19.wireOp",EDGE,"E90.top");var subQ1=sQuery(id+"F19.wireOp",EDGE,"E83");var subQ2=makeQuery(id+"F19.imprint","INTERSECT",VERTEX,{"derivedFrom":[subQ1,subQ0]});Q5=makeQuery(id+"F19.imprint","IMPRINT",FACE,{"disambiguationData":[TD([[makeQuery(id+"F19.imprint","IMPRINT",EDGE,{"disambiguationData":[TD([[subQ2,-1.0]])],"derivedFrom":subQ1}),1.0]])]});}
            var Q6;
            {var subQ0=sQuery(id+"F19.wireOp",EDGE,"E90.top");var subQ1=sQuery(id+"F19.wireOp",EDGE,"E83");var subQ2=makeQuery(id+"F19.imprint","INTERSECT",VERTEX,{"derivedFrom":[subQ1,subQ0]});Q6=makeQuery(id+"F19.imprint","IMPRINT",FACE,{"disambiguationData":[TD([[makeQuery(id+"F19.imprint","IMPRINT",EDGE,{"disambiguationData":[TD([[subQ2,-1.0]])],"derivedFrom":subQ1}),-1.0]])]});}
            var Q7;
            {var subQ0=sQuery(id+"F19.wireOp",EDGE,"E91.left");var subQ1=sQuery(id+"F19.wireOp",EDGE,"E84");var subQ2=makeQuery(id+"F19.imprint","INTERSECT",VERTEX,{"derivedFrom":[subQ1,subQ0]});Q7=makeQuery(id+"F19.imprint","IMPRINT",FACE,{"disambiguationData":[TD([[makeQuery(id+"F19.imprint","IMPRINT",EDGE,{"disambiguationData":[TD([[subQ2,-1.0]])],"derivedFrom":subQ1}),1.0]])]});}
            var Q8;
            {var subQ0=sQuery(id+"F19.wireOp",EDGE,"E91.left");var subQ1=sQuery(id+"F19.wireOp",EDGE,"E83");var subQ2=makeQuery(id+"F19.imprint","INTERSECT",VERTEX,{"derivedFrom":[subQ1,subQ0]});Q8=makeQuery(id+"F19.imprint","IMPRINT",FACE,{"disambiguationData":[TD([[makeQuery(id+"F19.imprint","IMPRINT",EDGE,{"disambiguationData":[TD([[subQ2,-1.0]])],"derivedFrom":subQ1}),1.0]])]});}
            var Q9;
            {var subQ0=sQuery(id+"F19.wireOp",EDGE,"E91.left");var subQ1=sQuery(id+"F19.wireOp",EDGE,"E83");var subQ2=makeQuery(id+"F19.imprint","INTERSECT",VERTEX,{"derivedFrom":[subQ1,subQ0]});Q9=makeQuery(id+"F19.imprint","IMPRINT",FACE,{"disambiguationData":[TD([[makeQuery(id+"F19.imprint","IMPRINT",EDGE,{"disambiguationData":[TD([[subQ2,-1.0]])],"derivedFrom":subQ1}),-1.0]])]});}
            var Q10;
            {var subQ5=sQuery(id+"F19.wireOp",EDGE,"DqG3VXCJ-E9Pa-22pF-3nJk-MnPQh88JCoLb");Q10=makeQuery(id+"F19.imprint","IMPRINT",FACE,{"disambiguationData":[TD([[makeQuery(id+"F19.imprint","IMPRINT",EDGE,{"derivedFrom":subQ5}),1.0]])]});}
            var Q11;
            Q11=makeQuery(id+"F19.imprint","IMPRINT",FACE,{"disambiguationData":[TD([[makeQuery(id+"F19.imprint","IMPRINT",EDGE,{"derivedFrom":sQuery(id+"F19.wireOp",EDGE,"E76")}),-1.0]])]});
            var Q12;
            {var subQ0=sQuery(id+"F19.wireOp",EDGE,"E90.bottom");var subQ1=sQuery(id+"F19.wireOp",EDGE,"E87");var subQ2=makeQuery(id+"F19.imprint","INTERSECT",VERTEX,{"derivedFrom":[subQ1,subQ0]});Q12=makeQuery(id+"F19.imprint","IMPRINT",FACE,{"disambiguationData":[TD([[makeQuery(id+"F19.imprint","IMPRINT",EDGE,{"disambiguationData":[TD([[subQ2,-1.0]])],"derivedFrom":subQ1}),-1.0]])]});}
            extrude(context, id + "F22", {"entities" : qUnion([Q0, Q1, Q2, Q3, Q4, Q5, Q6, Q7, Q8, Q9, Q10, Q11, Q12]), "operationType" : NewBodyOperationType.REMOVE, "depth" : 9.5 * mm, "offsetDistance" : 25 * mm});
        }
        {
            var Q0;
            Q0=makeQuery(id+"F12.imprint","IMPRINT",FACE,{"disambiguationData":[TD([[makeQuery(id+"F12.imprint","IMPRINT",EDGE,{"derivedFrom":sQuery(id+"F12.wireOp",EDGE,"E49")}),1.0]])]});
            extrude(context, id + "F23", {"entities" : qUnion([Q0]), "operationType" : NewBodyOperationType.REMOVE, "oppositeDirection" : true, "depth" : 25 * mm, "offsetDistance" : 25 * mm, "hasSecondDirection" : true, "secondDirectionOppositeDirection" : false, "secondDirectionDepth" : 25 * mm});
        }
        {
            var Q0;
            Q0=makeQuery(id+"F5.opExtrude","CAP_FACE",FACE,{"disambiguationData":[OSD([sQuery(id+"F2.wireOp",EDGE,"E5"),sQuery(id+"F2.wireOp",EDGE,"E12"),sQuery(id+"F4.wireOp",EDGE,"E14"),sQuery(id+"F4.wireOp",EDGE,"E21"),sQuery(id+"F4.wireOp",EDGE,"E24"),sQuery(id+"F4.wireOp",EDGE,"E25")])],"isStart":false});
            var sketch = newSketch(context, id + "F24", { "sketchPlane" : qUnion([Q0])});
            skLineSegment(sketch, "E98.bottom", {"start": v(-23.5, 13) * mm, "end": v(-55.3, 13) * mm});
            skLineSegment(sketch, "E98.top", {"start": v(-23.5, 43.45) * mm, "end": v(-55.3, 43.45) * mm});
            skLineSegment(sketch, "E98.left", {"start": v(-23.5, 13) * mm, "end": v(-23.5, 43.45) * mm});
            skLineSegment(sketch, "E98.right", {"start": v(-55.3, 13) * mm, "end": v(-55.3, 43.45) * mm});
            skLineSegment(sketch, "E99.bottom", {"start": v(23.5, 13) * mm, "end": v(53.46, 13) * mm});
            skLineSegment(sketch, "E99.top", {"start": v(23.5, 40.04) * mm, "end": v(53.46, 40.04) * mm});
            skLineSegment(sketch, "E99.left", {"start": v(23.5, 13) * mm, "end": v(23.5, 40.04) * mm});
            skLineSegment(sketch, "E99.right", {"start": v(53.46, 13) * mm, "end": v(53.46, 40.04) * mm});
            skPoint(sketch, "E100", {"position": v(0, 37.6) * mm});
            skPoint(sketch, "E101", {"position": v(23.5, 30) * mm});
            skPoint(sketch, "E102", {"position": v(-23.5, 30) * mm});
            skArc(sketch, "E103", {"start": v(-6.86, 40.64) * mm, "mid": v(-1.03, 45.03) * mm, "end": v(5.77, 42.4) * mm});
            skLineSegment(sketch, "E104", {"start": v(-23.5, 30) * mm, "end": v(-4.37, 43.7) * mm});
            skLineSegment(sketch, "E105", {"start": v(23.5, 30) * mm, "end": v(4.37, 43.7) * mm});
            skLineSegment(sketch, "E106", {"start": v(23.5, 40.04) * mm, "end": v(4.37, 50.22) * mm});
            skLineSegment(sketch, "E107", {"start": v(4.37, 50.22) * mm, "end": v(-6.86, 50.22) * mm});
            skLineSegment(sketch, "E108", {"start": v(-6.86, 50.22) * mm, "end": v(-23.5, 43.45) * mm});
            skSolve(sketch);
        }
        {
            var Q0;
            Q0=qCreatedBy(makeId("Top.planeOp"),FACE);
            var sketch = newSketch(context, id + "F25", { "sketchPlane" : qUnion([Q0])});
            skCircle(sketch, "E109", {"center": v(0, 9.8) * mm, "radius": 4 * mm});
            skCircle(sketch, "E110", {"center": v(0, 9.8) * mm, "radius": 2 * mm});
            skCircle(sketch, "E111", {"center": v(0, -18.41) * mm, "radius": 4 * mm});
            skCircle(sketch, "E112", {"center": v(0, -18.41) * mm, "radius": 2 * mm});
            skSolve(sketch);
        }
        {
            var Q0;
            Q0=makeQuery(id+"F25.imprint","IMPRINT",FACE,{"disambiguationData":[TD([[makeQuery(id+"F25.imprint","IMPRINT",EDGE,{"derivedFrom":sQuery(id+"F25.wireOp",EDGE,"E109")}),1.0]])]});
            extrude(context, id + "F26", {"entities" : qUnion([Q0]), "depth" : 370 * mm, "offsetDistance" : 25 * mm, "symmetric" : true});
        }
        {
            var Q0;
            {var subQ2=sQuery(id+"F24.wireOp",EDGE,"E98.top");Q0=makeQuery(id+"F24.imprint","IMPRINT",FACE,{"disambiguationData":[TD([[makeQuery(id+"F24.imprint","IMPRINT",EDGE,{"derivedFrom":subQ2}),1.0]])]});}
            var Q1;
            {var subQ2=sQuery(id+"F24.wireOp",EDGE,"E99.top");Q1=makeQuery(id+"F24.imprint","IMPRINT",FACE,{"disambiguationData":[TD([[makeQuery(id+"F24.imprint","IMPRINT",EDGE,{"derivedFrom":subQ2}),-1.0]])]});}
            var Q2;
            {var subQ0=sQuery(id+"F24.wireOp",EDGE,"E99.left");var subQ6=sQuery(id+"F24.wireOp",EDGE,"E99.bottom");var subQ11=makeQuery(id+"F24.imprint","INTERSECT",VERTEX,{"derivedFrom":[subQ6,subQ0]});Q2=makeQuery(id+"F24.imprint","IMPRINT",FACE,{"disambiguationData":[TD([[makeQuery(id+"F24.imprint","IMPRINT",EDGE,{"disambiguationData":[TD([[subQ11,1.0]])],"derivedFrom":subQ6}),-1.0]])]});}
            var Q3;
            {var subQ5=makeQuery(id+"F5.opExtrude","CAP_EDGE",EDGE,{"disambiguationData":[OSD([sQuery(id+"F4.wireOp",EDGE,"E25")])],"isStart":false});var subQ8=sQuery(id+"F24.wireOp",EDGE,"E98.bottom");var subQ9=makeQuery(id+"F24.imprint","INTERSECT",VERTEX,{"derivedFrom":[subQ5,subQ8]});Q3=makeQuery(id+"F24.imprint","IMPRINT",FACE,{"disambiguationData":[TD([[makeQuery(id+"F24.imprint","IMPRINT",EDGE,{"disambiguationData":[TD([[subQ9,1.0]])],"derivedFrom":subQ8}),-1.0]])]});}
            var Q4;
            {var subQ4=sQuery(id+"F24.wireOp",EDGE,"E106");Q4=makeQuery(id+"F24.imprint","IMPRINT",FACE,{"disambiguationData":[TD([[makeQuery(id+"F24.imprint","IMPRINT",EDGE,{"derivedFrom":subQ4}),1.0]])]});}
            var Q5;
            {var subQ0=sQuery(id+"F24.wireOp",EDGE,"E104");Q5=makeQuery(id+"F24.imprint","IMPRINT",FACE,{"disambiguationData":[TD([[makeQuery(id+"F24.imprint","IMPRINT",EDGE,{"derivedFrom":subQ0}),1.0]])]});}
            extrude(context, id + "F27", {"entities" : qUnion([Q0, Q1, Q2, Q3, Q4, Q5]), "operationType" : NewBodyOperationType.REMOVE, "oppositeDirection" : true, "depth" : 25 * mm, "offsetDistance" : 25 * mm});
        }
        {
            var Q0;
            Q0=makeQuery(id+"F7.opExtrude","CAP_FACE",FACE,{"disambiguationData":[OSD([sQuery(id+"F6.wireOp",EDGE,"E29"),sQuery(id+"F6.wireOp",EDGE,"E30"),sQuery(id+"F6.wireOp",EDGE,"E32"),sQuery(id+"F6.wireOp",EDGE,"E33"),sQuery(id+"F6.wireOp",EDGE,"E34.left"),sQuery(id+"F6.wireOp",EDGE,"E39"),sQuery(id+"F6.wireOp",EDGE,"E40"),sQuery(id+"F6.wireOp",EDGE,"E41")])],"isStart":true});
            var sketch = newSketch(context, id + "F28", { "sketchPlane" : qUnion([Q0])});
            skLineSegment(sketch, "E113", {"start": v(74.75, 23.5) * mm, "end": v(74.75, 20.34) * mm});
            skLineSegment(sketch, "E114", {"start": v(74.75, 23.5) * mm, "end": v(65, 23.5) * mm});
            skLineSegment(sketch, "E115", {"start": v(65, 23.5) * mm, "end": v(65, 18.92) * mm});
            skLineSegment(sketch, "E116", {"start": v(65, -19.22) * mm, "end": v(65, -23.5) * mm});
            skLineSegment(sketch, "E117", {"start": v(65, -23.5) * mm, "end": v(74.75, -23.5) * mm});
            skLineSegment(sketch, "E118", {"start": v(74.75, -23.5) * mm, "end": v(74.75, -20.34) * mm});
            skArc(sketch, "E119", {"start": v(74.75, -20.34) * mm, "mid": v(69.74, -20.93) * mm, "end": v(65, -19.22) * mm});
            skArc(sketch, "E120", {"start": v(74.75, 20.34) * mm, "mid": v(69.74, 20.93) * mm, "end": v(65, 19.22) * mm});
            skArc(sketch, "E121", {"start": v(75.58, 0) * mm, "mid": v(79.57, 3.1) * mm, "end": v(81.75, 7.67) * mm});
            skArc(sketch, "E122", {"start": v(75.58, 0) * mm, "mid": v(79.57, -3.1) * mm, "end": v(81.75, -7.67) * mm});
            skLineSegment(sketch, "E123", {"start": v(81.75, -7.67) * mm, "end": v(84.5, -20.34) * mm});
            skLineSegment(sketch, "E124", {"start": v(84.5, -20.34) * mm, "end": v(84.5, 20.34) * mm});
            skLineSegment(sketch, "E125", {"start": v(84.5, 20.34) * mm, "end": v(81.75, 7.67) * mm});
            skSolve(sketch);
        }
        {
            var Q0;
            Q0=makeQuery(id+"F28.imprint","IMPRINT",FACE,{"disambiguationData":[TD([[makeQuery(id+"F28.imprint","IMPRINT",EDGE,{"derivedFrom":sQuery(id+"F28.wireOp",EDGE,"E113")}),-1.0]])]});
            var Q1;
            Q1=makeQuery(id+"F28.imprint","IMPRINT",FACE,{"disambiguationData":[TD([[makeQuery(id+"F28.imprint","IMPRINT",EDGE,{"derivedFrom":sQuery(id+"F28.wireOp",EDGE,"E121")}),-1.0]])]});
            var Q2;
            Q2=makeQuery(id+"F28.imprint","IMPRINT",FACE,{"disambiguationData":[TD([[makeQuery(id+"F28.imprint","IMPRINT",EDGE,{"derivedFrom":sQuery(id+"F28.wireOp",EDGE,"E116")}),-1.0]])]});
            extrude(context, id + "F29", {"entities" : qUnion([Q0, Q1, Q2]), "operationType" : NewBodyOperationType.ADD, "depth" : 10 * mm, "offsetDistance" : 25 * mm});
        }
        {
            var Q0;
            Q0=makeQuery(id+"F3.opExtrude","SWEPT_BODY",BODY,{"disambiguationData":[OSD([sQuery(id+"F2.wireOp",EDGE,"E1"),sQuery(id+"F2.wireOp",EDGE,"E5"),sQuery(id+"F2.wireOp",EDGE,"E6"),sQuery(id+"F2.wireOp",EDGE,"E7"),sQuery(id+"F2.wireOp",EDGE,"E9"),sQuery(id+"F2.wireOp",EDGE,"E10"),sQuery(id+"F2.wireOp",EDGE,"E12"),sQuery(id+"F2.wireOp",EDGE,"E13")])]});
            var Q1;
            Q1=makeQuery(id+"F13.opExtrude","SWEPT_BODY",BODY,{"disambiguationData":[OSD([sQuery(id+"F12.wireOp",EDGE,"E44"),sQuery(id+"F12.wireOp",EDGE,"E45"),sQuery(id+"F12.wireOp",EDGE,"E46"),sQuery(id+"F12.wireOp",EDGE,"E49"),sQuery(id+"F12.wireOp",EDGE,"E50")])]});
            var Q2;
            Q2=makeQuery(id+"F20.opExtrude","SWEPT_BODY",BODY,{"disambiguationData":[OSD([sQuery(id+"F19.wireOp",EDGE,"E76"),sQuery(id+"F19.wireOp",EDGE,"E77"),sQuery(id+"F19.wireOp",EDGE,"E78"),sQuery(id+"F19.wireOp",EDGE,"E79"),sQuery(id+"F19.wireOp",EDGE,"E87"),sQuery(id+"F19.wireOp",EDGE,"E88"),sQuery(id+"F19.wireOp",EDGE,"E89"),sQuery(id+"F19.wireOp",EDGE,"E90.bottom"),sQuery(id+"F19.wireOp",EDGE,"E90.top"),sQuery(id+"F19.wireOp",EDGE,"E91.left"),sQuery(id+"F19.wireOp",EDGE,"E91.right"),sQuery(id+"F19.wireOp",EDGE,"E94"),sQuery(id+"F19.wireOp",EDGE,"E95.bottom"),sQuery(id+"F19.wireOp",EDGE,"E95.top")])]});
            var Q3;
            Q3=qCreatedBy(makeId("Right.planeOp"),FACE);
            mirror(context, id + "F30", {"entities" : qUnion([Q0, Q1, Q2]), "mirrorPlane" : qUnion([Q3])});
        }
        {
            var Q0;
            Q0=qCreatedBy(makeId("Right.planeOp"),FACE);
            var sketch = newSketch(context, id + "F31", { "sketchPlane" : qUnion([Q0])});
            skPoint(sketch, "E126", {"position": v(0, 37.6) * mm});
            skPoint(sketch, "E127", {"position": v(0, -17.4) * mm});
            skPoint(sketch, "E128", {"position": v(10, 13) * mm});
            skPoint(sketch, "E129", {"position": v(-10, 13) * mm});
            skLineSegment(sketch, "E130", {"start": v(10, 13) * mm, "end": v(4, 13) * mm, "construction": true});
            skLineSegment(sketch, "E131", {"start": v(-10, 13) * mm, "end": v(-4, 13) * mm, "construction": true});
            skPoint(sketch, "E132", {"position": v(-3, 13) * mm});
            skPoint(sketch, "E133", {"position": v(2, 13) * mm});
            skLineSegment(sketch, "E134", {"start": v(4, 13) * mm, "end": v(2, 13) * mm, "construction": true});
            skLineSegment(sketch, "E135", {"start": v(-3, 13) * mm, "end": v(-5, 13) * mm, "construction": true});
            skCircle(sketch, "E136", {"center": v(0, 37.6) * mm, "radius": 7.5 * mm, "construction": true});
            skCircle(sketch, "E137", {"center": v(0, 37.6) * mm, "radius": 11 * mm, "construction": true});
            skCircle(sketch, "E138", {"center": v(0, -17.4) * mm, "radius": 11 * mm, "construction": true});
            skCircle(sketch, "E139", {"center": v(0, -17.4) * mm, "radius": 7.5 * mm});
            skLineSegment(sketch, "E140", {"start": v(-5, 13) * mm, "end": v(-5, -7.6) * mm});
            skLineSegment(sketch, "E141", {"start": v(-9, 31.28) * mm, "end": v(-9, -11.08) * mm});
            skArc(sketch, "E142", {"start": v(-9, 31.28) * mm, "mid": v(6.79, 46.25) * mm, "end": v(-4, 27.35) * mm});
            skCircle(sketch, "E143", {"center": v(0, 37.6) * mm, "radius": 7.5 * mm});
            skArc(sketch, "E144", {"start": v(-5, -7.6) * mm, "mid": v(7.21, -25.7) * mm, "end": v(-9, -11.08) * mm});
            skLineSegment(sketch, "E145", {"start": v(11, 37.6) * mm, "end": v(11, -17.4) * mm});
            skLineSegment(sketch, "E146.top", {"start": v(5, 17) * mm, "end": v(-5, 17) * mm});
            skLineSegment(sketch, "E146.left", {"start": v(5, 26.5) * mm, "end": v(5, 17) * mm});
            skLineSegment(sketch, "E146.right", {"start": v(-5, 26.5) * mm, "end": v(-5, 17) * mm});
            skPoint(sketch, "E147", {"position": v(5, 26.5) * mm});
            skPoint(sketch, "E148", {"position": v(5, 17) * mm});
            skLineSegment(sketch, "E149", {"start": v(-5, 13) * mm, "end": v(-5, 17) * mm});
            skLineSegment(sketch, "E150", {"start": v(-5, 26.5) * mm, "end": v(-5, 27.8) * mm});
            skArc(sketch, "E151", {"start": v(-4, 27.35) * mm, "mid": v(-4.5, 27.57) * mm, "end": v(-5, 27.8) * mm});
            skLineSegment(sketch, "E152", {"start": v(5, 25.6) * mm, "end": v(-0.39, 25.6) * mm});
            skLineSegment(sketch, "E153", {"start": v(-0.39, 25.6) * mm, "end": v(-0.39, 28.1) * mm});
            skLineSegment(sketch, "E154", {"start": v(-0.39, 28.1) * mm, "end": v(-5, 28.1) * mm});
            skLineSegment(sketch, "E155", {"start": v(-5, 28.1) * mm, "end": v(-5, 27.8) * mm});
            skLineSegment(sketch, "E156", {"start": v(5, 26.5) * mm, "end": v(-5, 26.5) * mm});
            skLineSegment(sketch, "E157", {"start": v(-0.39, 25.6) * mm, "end": v(0, 25.6) * mm});
            skLineSegment(sketch, "E158", {"start": v(0, 25.6) * mm, "end": v(2.33, 25.6) * mm});
            skLineSegment(sketch, "E159", {"start": v(2.33, 25.6) * mm, "end": v(2.33, 26.85) * mm});
            skSolve(sketch);
        }
        {
            var Q0;
            Q0=makeQuery(id+"F31.imprint","IMPRINT",FACE,{"disambiguationData":[TD([[makeQuery(id+"F31.imprint","IMPRINT",EDGE,{"derivedFrom":sQuery(id+"F31.wireOp",EDGE,"E139")}),-1.0]])]});
            var Q1;
            {var subQ1=sQuery(id+"F31.wireOp",EDGE,"s4j5GkUa-E5M7-RjrF-nGWZ-R8OBUKVPGPec");Q1=makeQuery(id+"F31.imprint","IMPRINT",FACE,{"disambiguationData":[TD([[makeQuery(id+"F31.imprint","IMPRINT",EDGE,{"derivedFrom":subQ1}),1.0]])]});}
            var Q2;
            {var subQ1=sQuery(id+"F31.wireOp",EDGE,"E140");Q2=makeQuery(id+"F31.imprint","IMPRINT",FACE,{"disambiguationData":[TD([[makeQuery(id+"F31.imprint","IMPRINT",EDGE,{"derivedFrom":subQ1}),1.0]])]});}
            var Q3;
            {var subQ0=sQuery(id+"F31.wireOp",EDGE,"E153");var subQ1=sQuery(id+"F31.wireOp",EDGE,"E142");var subQ2=makeQuery(id+"F31.imprint","INTERSECT",VERTEX,{"derivedFrom":[subQ1,subQ0]});Q3=makeQuery(id+"F31.imprint","IMPRINT",FACE,{"disambiguationData":[TD([[makeQuery(id+"F31.imprint","IMPRINT",EDGE,{"disambiguationData":[TD([[subQ2,1.0]])],"derivedFrom":subQ1}),1.0]])]});}
            var Q4;
            {var subQ5=sQuery(id+"F31.wireOp",EDGE,"E152");var subQ7=makeQuery(id+"F31.imprint","IMPRINT",VERTEX,{"derivedFrom":subQ5});Q4=makeQuery(id+"F31.imprint","IMPRINT",FACE,{"disambiguationData":[TD([[makeQuery(id+"F31.imprint","IMPRINT",EDGE,{"disambiguationData":[TD([[subQ7,1.0]])],"derivedFrom":subQ5}),-1.0]])]});}
            extrude(context, id + "F32", {"entities" : qUnion([Q0, Q1, Q2, Q3, Q4]), "depth" : 50 * mm, "offsetDistance" : 25 * mm, "symmetric" : true});
        }
        {
            var Q0;
            {var subQ1=sQuery(id+"F31.wireOp",EDGE,"E140");Q0=makeQuery(id+"F31.imprint","IMPRINT",FACE,{"disambiguationData":[TD([[makeQuery(id+"F31.imprint","IMPRINT",EDGE,{"derivedFrom":subQ1}),1.0]])]});}
            var Q1;
            {var subQ4=sQuery(id+"F31.wireOp",EDGE,"E151");Q1=makeQuery(id+"F31.imprint","IMPRINT",FACE,{"disambiguationData":[TD([[makeQuery(id+"F31.imprint","IMPRINT",EDGE,{"derivedFrom":subQ4}),-1.0]])]});}
            var Q2;
            {var subQ5=sQuery(id+"F31.wireOp",EDGE,"E146.top");Q2=makeQuery(id+"F31.imprint","IMPRINT",FACE,{"disambiguationData":[TD([[makeQuery(id+"F31.imprint","IMPRINT",EDGE,{"derivedFrom":subQ5}),-1.0]])]});}
            extrude(context, id + "F33", {"entities" : qUnion([Q0, Q1, Q2]), "operationType" : NewBodyOperationType.REMOVE, "oppositeDirection" : true, "depth" : ((50 - (2 * 3.5))) * mm, "offsetDistance" : 25 * mm, "symmetric" : true});
        }
        {
            var Q0;
            Q0=qCreatedBy(makeId("Top.planeOp"),FACE);
            var sketch = newSketch(context, id + "F34", { "sketchPlane" : qUnion([Q0])});
            skPoint(sketch, "E160", {"position": v(0, -5) * mm});
            skLineSegment(sketch, "E161", {"start": v(0, -6.97) * mm, "end": v(21, -6.97) * mm});
            skLineSegment(sketch, "E162", {"start": v(0, -6.97) * mm, "end": v(-21, -6.97) * mm});
            skLineSegment(sketch, "E163", {"start": v(-21, -6.97) * mm, "end": v(-21, -4.2) * mm});
            skLineSegment(sketch, "E164", {"start": v(-21, -4.2) * mm, "end": v(-20.86, -3.4) * mm});
            skLineSegment(sketch, "E165", {"start": v(-20.01, -3.4) * mm, "end": v(-19.87, -4.2) * mm});
            skLineSegment(sketch, "E166", {"start": v(-19.87, -4.2) * mm, "end": v(-19, -4.2) * mm});
            skLineSegment(sketch, "E167.1.0.0", {"start": v(-19, -4.2) * mm, "end": v(-18.86, -3.4) * mm});
            skLineSegment(sketch, "E167.1.0.1", {"start": v(-18.86, -3.4) * mm, "end": v(-18.01, -3.4) * mm});
            skLineSegment(sketch, "E167.1.0.2", {"start": v(-18.01, -3.4) * mm, "end": v(-17.87, -4.2) * mm});
            skLineSegment(sketch, "E167.1.0.3", {"start": v(-17.87, -4.2) * mm, "end": v(-17, -4.2) * mm});
            skLineSegment(sketch, "E167.2.0.0", {"start": v(-17, -4.2) * mm, "end": v(-16.86, -3.4) * mm});
            skLineSegment(sketch, "E167.2.0.1", {"start": v(-16.86, -3.4) * mm, "end": v(-16.01, -3.4) * mm});
            skLineSegment(sketch, "E167.2.0.2", {"start": v(-16.01, -3.4) * mm, "end": v(-15.87, -4.2) * mm});
            skLineSegment(sketch, "E167.2.0.3", {"start": v(-15.87, -4.2) * mm, "end": v(-15, -4.2) * mm});
            skLineSegment(sketch, "E167.3.0.0", {"start": v(-15, -4.2) * mm, "end": v(-14.86, -3.4) * mm});
            skLineSegment(sketch, "E167.3.0.1", {"start": v(-14.86, -3.4) * mm, "end": v(-14.01, -3.4) * mm});
            skLineSegment(sketch, "E167.3.0.2", {"start": v(-14.01, -3.4) * mm, "end": v(-13.87, -4.2) * mm});
            skLineSegment(sketch, "E167.3.0.3", {"start": v(-13.87, -4.2) * mm, "end": v(-13, -4.2) * mm});
            skLineSegment(sketch, "E167.4.0.0", {"start": v(-13, -4.2) * mm, "end": v(-12.86, -3.4) * mm});
            skLineSegment(sketch, "E167.4.0.1", {"start": v(-12.86, -3.4) * mm, "end": v(-12.01, -3.4) * mm});
            skLineSegment(sketch, "E167.4.0.2", {"start": v(-12.01, -3.4) * mm, "end": v(-11.87, -4.2) * mm});
            skLineSegment(sketch, "E167.4.0.3", {"start": v(-11.87, -4.2) * mm, "end": v(-11, -4.2) * mm});
            skLineSegment(sketch, "E167.5.0.0", {"start": v(-11, -4.2) * mm, "end": v(-10.86, -3.4) * mm});
            skLineSegment(sketch, "E167.5.0.1", {"start": v(-10.86, -3.4) * mm, "end": v(-10.01, -3.4) * mm});
            skLineSegment(sketch, "E167.5.0.2", {"start": v(-10.01, -3.4) * mm, "end": v(-9.87, -4.2) * mm});
            skLineSegment(sketch, "E167.5.0.3", {"start": v(-9.87, -4.2) * mm, "end": v(-9, -4.2) * mm});
            skLineSegment(sketch, "E167.6.0.0", {"start": v(-9, -4.2) * mm, "end": v(-8.86, -3.4) * mm});
            skLineSegment(sketch, "E167.6.0.1", {"start": v(-8.86, -3.4) * mm, "end": v(-8.01, -3.4) * mm});
            skLineSegment(sketch, "E167.6.0.2", {"start": v(-8.01, -3.4) * mm, "end": v(-7.87, -4.2) * mm});
            skLineSegment(sketch, "E167.6.0.3", {"start": v(-7.87, -4.2) * mm, "end": v(-7, -4.2) * mm});
            skLineSegment(sketch, "E167.7.0.0", {"start": v(-7, -4.2) * mm, "end": v(-6.86, -3.4) * mm});
            skLineSegment(sketch, "E167.7.0.1", {"start": v(-6.86, -3.4) * mm, "end": v(-6.01, -3.4) * mm});
            skLineSegment(sketch, "E167.7.0.2", {"start": v(-6.01, -3.4) * mm, "end": v(-5.87, -4.2) * mm});
            skLineSegment(sketch, "E167.7.0.3", {"start": v(-5.87, -4.2) * mm, "end": v(-5, -4.2) * mm});
            skLineSegment(sketch, "E167.8.0.0", {"start": v(-5, -4.2) * mm, "end": v(-4.86, -3.4) * mm});
            skLineSegment(sketch, "E167.8.0.1", {"start": v(-4.86, -3.4) * mm, "end": v(-4.01, -3.4) * mm});
            skLineSegment(sketch, "E167.8.0.2", {"start": v(-4.01, -3.4) * mm, "end": v(-3.87, -4.2) * mm});
            skLineSegment(sketch, "E167.8.0.3", {"start": v(-3.87, -4.2) * mm, "end": v(-3, -4.2) * mm});
            skLineSegment(sketch, "E167.9.0.0", {"start": v(-3, -4.2) * mm, "end": v(-2.86, -3.4) * mm});
            skLineSegment(sketch, "E167.9.0.1", {"start": v(-2.86, -3.4) * mm, "end": v(-2.01, -3.4) * mm});
            skLineSegment(sketch, "E167.9.0.2", {"start": v(-2.01, -3.4) * mm, "end": v(-1.87, -4.2) * mm});
            skLineSegment(sketch, "E167.9.0.3", {"start": v(-1.87, -4.2) * mm, "end": v(-1, -4.2) * mm});
            skLineSegment(sketch, "E167.10.0.0", {"start": v(-1, -4.2) * mm, "end": v(-0.86, -3.4) * mm});
            skLineSegment(sketch, "E167.10.0.1", {"start": v(-0.86, -3.4) * mm, "end": v(-0.01, -3.4) * mm});
            skLineSegment(sketch, "E167.10.0.2", {"start": v(-0.01, -3.4) * mm, "end": v(0.13, -4.2) * mm});
            skLineSegment(sketch, "E167.10.0.3", {"start": v(0.13, -4.2) * mm, "end": v(1, -4.2) * mm});
            skLineSegment(sketch, "E167.11.0.0", {"start": v(1, -4.2) * mm, "end": v(1.14, -3.4) * mm});
            skLineSegment(sketch, "E167.11.0.1", {"start": v(1.14, -3.4) * mm, "end": v(1.99, -3.4) * mm});
            skLineSegment(sketch, "E167.11.0.2", {"start": v(1.99, -3.4) * mm, "end": v(2.13, -4.2) * mm});
            skLineSegment(sketch, "E167.11.0.3", {"start": v(2.13, -4.2) * mm, "end": v(3, -4.2) * mm});
            skLineSegment(sketch, "E167.12.0.0", {"start": v(3, -4.2) * mm, "end": v(3.14, -3.4) * mm});
            skLineSegment(sketch, "E167.12.0.1", {"start": v(3.14, -3.4) * mm, "end": v(3.99, -3.4) * mm});
            skLineSegment(sketch, "E167.12.0.2", {"start": v(3.99, -3.4) * mm, "end": v(4.13, -4.2) * mm});
            skLineSegment(sketch, "E167.12.0.3", {"start": v(4.13, -4.2) * mm, "end": v(5, -4.2) * mm});
            skLineSegment(sketch, "E167.13.0.0", {"start": v(5, -4.2) * mm, "end": v(5.14, -3.4) * mm});
            skLineSegment(sketch, "E167.13.0.1", {"start": v(5.14, -3.4) * mm, "end": v(5.99, -3.4) * mm});
            skLineSegment(sketch, "E167.13.0.2", {"start": v(5.99, -3.4) * mm, "end": v(6.13, -4.2) * mm});
            skLineSegment(sketch, "E167.13.0.3", {"start": v(6.13, -4.2) * mm, "end": v(7, -4.2) * mm});
            skLineSegment(sketch, "E167.14.0.0", {"start": v(7, -4.2) * mm, "end": v(7.14, -3.4) * mm});
            skLineSegment(sketch, "E167.14.0.1", {"start": v(7.14, -3.4) * mm, "end": v(7.99, -3.4) * mm});
            skLineSegment(sketch, "E167.14.0.2", {"start": v(7.99, -3.4) * mm, "end": v(8.13, -4.2) * mm});
            skLineSegment(sketch, "E167.14.0.3", {"start": v(8.13, -4.2) * mm, "end": v(9, -4.2) * mm});
            skLineSegment(sketch, "E167.15.0.0", {"start": v(9, -4.2) * mm, "end": v(9.14, -3.4) * mm});
            skLineSegment(sketch, "E167.15.0.1", {"start": v(9.14, -3.4) * mm, "end": v(9.99, -3.4) * mm});
            skLineSegment(sketch, "E167.15.0.2", {"start": v(9.99, -3.4) * mm, "end": v(10.13, -4.2) * mm});
            skLineSegment(sketch, "E167.15.0.3", {"start": v(10.13, -4.2) * mm, "end": v(11, -4.2) * mm});
            skLineSegment(sketch, "E167.16.0.0", {"start": v(11, -4.2) * mm, "end": v(11.14, -3.4) * mm});
            skLineSegment(sketch, "E167.16.0.1", {"start": v(11.14, -3.4) * mm, "end": v(11.99, -3.4) * mm});
            skLineSegment(sketch, "E167.16.0.2", {"start": v(11.99, -3.4) * mm, "end": v(12.13, -4.2) * mm});
            skLineSegment(sketch, "E167.16.0.3", {"start": v(12.13, -4.2) * mm, "end": v(13, -4.2) * mm});
            skLineSegment(sketch, "E167.17.0.0", {"start": v(13, -4.2) * mm, "end": v(13.14, -3.4) * mm});
            skLineSegment(sketch, "E167.17.0.1", {"start": v(13.14, -3.4) * mm, "end": v(13.99, -3.4) * mm});
            skLineSegment(sketch, "E167.17.0.2", {"start": v(13.99, -3.4) * mm, "end": v(14.13, -4.2) * mm});
            skLineSegment(sketch, "E167.17.0.3", {"start": v(14.13, -4.2) * mm, "end": v(15, -4.2) * mm});
            skLineSegment(sketch, "E167.18.0.0", {"start": v(15, -4.2) * mm, "end": v(15.14, -3.4) * mm});
            skLineSegment(sketch, "E167.18.0.1", {"start": v(15.14, -3.4) * mm, "end": v(15.99, -3.4) * mm});
            skLineSegment(sketch, "E167.18.0.2", {"start": v(15.99, -3.4) * mm, "end": v(16.13, -4.2) * mm});
            skLineSegment(sketch, "E167.18.0.3", {"start": v(16.13, -4.2) * mm, "end": v(17, -4.2) * mm});
            skLineSegment(sketch, "E167.19.0.0", {"start": v(17, -4.2) * mm, "end": v(17.14, -3.4) * mm});
            skLineSegment(sketch, "E167.19.0.1", {"start": v(17.14, -3.4) * mm, "end": v(17.99, -3.4) * mm});
            skLineSegment(sketch, "E167.19.0.2", {"start": v(17.99, -3.4) * mm, "end": v(18.13, -4.2) * mm});
            skLineSegment(sketch, "E167.19.0.3", {"start": v(18.13, -4.2) * mm, "end": v(19, -4.2) * mm});
            skLineSegment(sketch, "E167.20.0.0", {"start": v(19, -4.2) * mm, "end": v(19.14, -3.4) * mm});
            skLineSegment(sketch, "E167.20.0.1", {"start": v(19.14, -3.4) * mm, "end": v(19.99, -3.4) * mm});
            skLineSegment(sketch, "E167.20.0.2", {"start": v(19.99, -3.4) * mm, "end": v(20.13, -4.2) * mm});
            skLineSegment(sketch, "E167.20.0.3", {"start": v(20.13, -4.2) * mm, "end": v(21, -4.2) * mm});
            skLineSegment(sketch, "E167.direction1", {"start": v(-21, -4.2) * mm, "end": v(-19, -4.2) * mm, "construction": true});
            skLineSegment(sketch, "E168", {"start": v(21, -6.97) * mm, "end": v(21, -4.2) * mm});
            skLineSegment(sketch, "E169", {"start": v(-20.7, -3.4) * mm, "end": v(-20.17, -3.4) * mm});
            skArc(sketch, "E170", {"start": v(-20.7, -3.4) * mm, "mid": v(-20.82, -3.44) * mm, "end": v(-20.89, -3.55) * mm});
            skArc(sketch, "E171", {"start": v(-20.17, -3.4) * mm, "mid": v(-20.05, -3.44) * mm, "end": v(-19.99, -3.55) * mm});
            skLineSegment(sketch, "E172", {"start": v(-20.89, -3.55) * mm, "end": v(-19.99, -3.55) * mm, "construction": true});
            skSolve(sketch);
        }
        {
            var Q0;
            Q0=makeQuery(id+"F34.imprint","IMPRINT",FACE,{"disambiguationData":[TD([[makeQuery(id+"F34.imprint","IMPRINT",EDGE,{"derivedFrom":sQuery(id+"F34.wireOp",EDGE,"E161")}),1.0]])]});
            extrude(context, id + "F35", {"entities" : qUnion([Q0]), "operationType" : NewBodyOperationType.ADD, "depth" : 29 * mm, "offsetDistance" : 25 * mm, "hasSecondDirection" : true, "secondDirectionOppositeDirection" : false, "secondDirectionDepth" : 17 * mm});
        }
        {
            var Q0;
            Q0=qCreatedBy(makeId("Right.planeOp"),FACE);
            var sketch = newSketch(context, id + "F36", { "sketchPlane" : qUnion([Q0])});
            skLineSegment(sketch, "E173", {"start": v(-0.49, 25.3) * mm, "end": v(-0.49, 27.6) * mm});
            skLineSegment(sketch, "E174", {"start": v(-0.49, 27.6) * mm, "end": v(-2.55, 27.6) * mm});
            skLineSegment(sketch, "E175", {"start": v(-2.55, 27.6) * mm, "end": v(-2.55, 17.5) * mm});
            skLineSegment(sketch, "E176", {"start": v(-2.55, 17.5) * mm, "end": v(-0.49, 17.5) * mm});
            skLineSegment(sketch, "E177", {"start": v(-0.49, 17.5) * mm, "end": v(-0.49, 19.8) * mm});
            skLineSegment(sketch, "E178", {"start": v(-0.49, 19.8) * mm, "end": v(1.45, 19.8) * mm});
            skLineSegment(sketch, "E179", {"start": v(1.45, 19.8) * mm, "end": v(1.45, 25.3) * mm});
            skLineSegment(sketch, "E180", {"start": v(1.45, 25.3) * mm, "end": v(-0.49, 25.3) * mm});
            skPoint(sketch, "E181", {"position": v(-3.55, 22.55) * mm});
            skPoint(sketch, "E182", {"position": v(1.45, 22.55) * mm});
            skPoint(sketch, "E183", {"position": v(-2.55, 22.55) * mm});
            skSolve(sketch);
        }
        {
            var Q0;
            Q0=makeQuery(id+"F36.imprint","IMPRINT",FACE,{"disambiguationData":[TD([[makeQuery(id+"F36.imprint","IMPRINT",EDGE,{"derivedFrom":sQuery(id+"F36.wireOp",EDGE,"E173")}),1.0]])]});
            extrude(context, id + "F37", {"entities" : qUnion([Q0]), "depth" : 50 * mm, "offsetDistance" : 25 * mm, "symmetric" : true});
        }
    });
